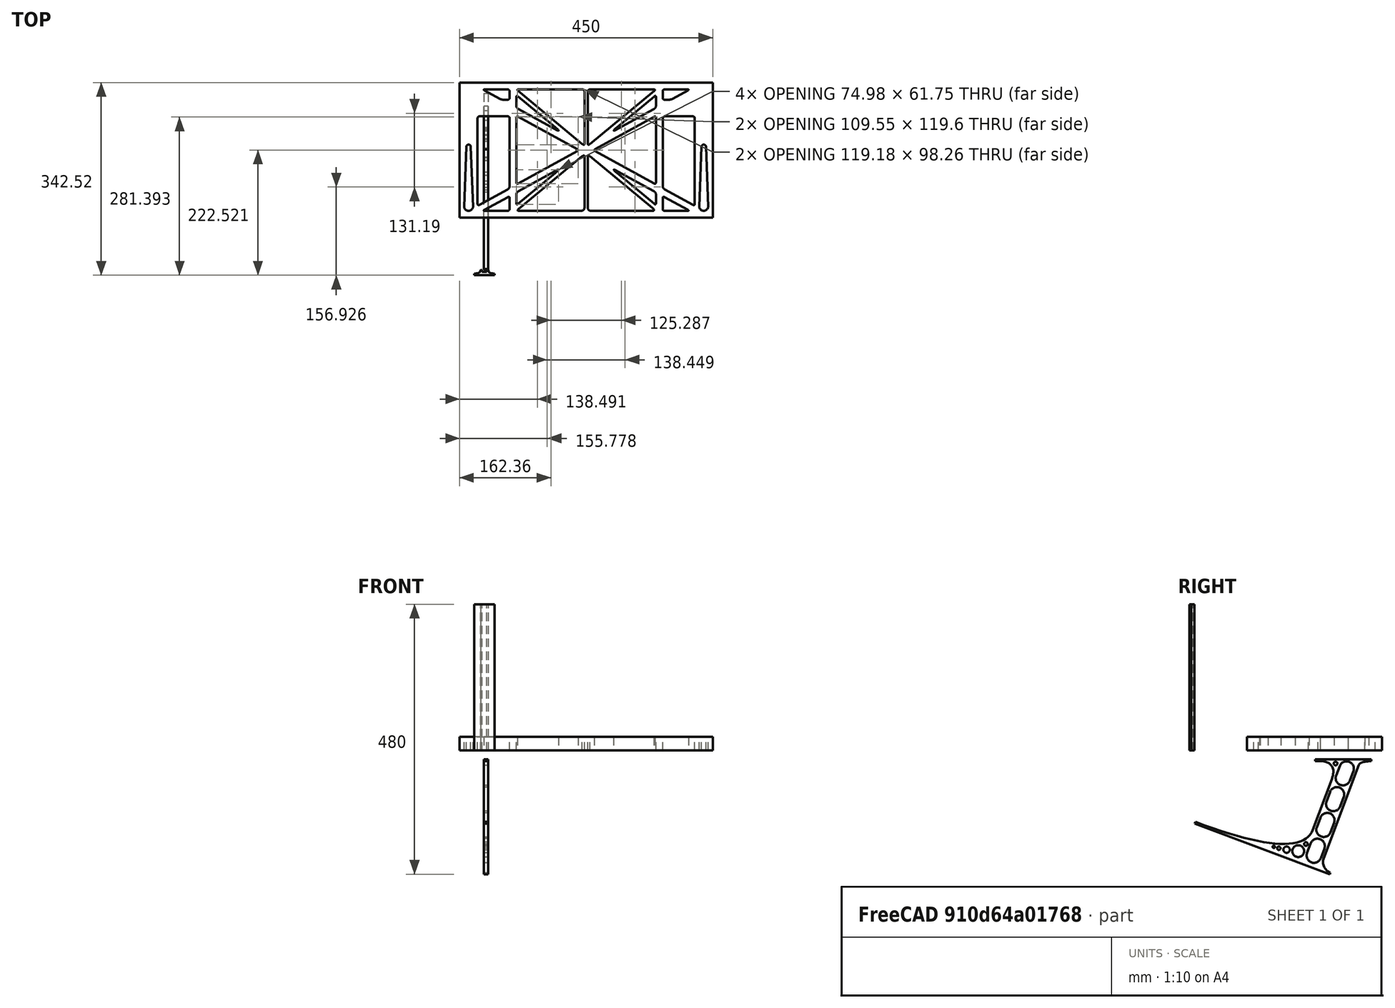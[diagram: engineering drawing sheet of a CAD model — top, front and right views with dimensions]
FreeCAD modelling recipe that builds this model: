
FCSTD DOCUMENT  (FreeCAD 0.19R0.19.2)
Label: laptopStand151FCStd
License: All rights reserved
LicenseURL: http://en.wikipedia.org/wiki/All_rights_reserved
objects: Sketcher::SketchObject×4, Part::Extrusion×3
note: 7 computed .brp shape members not serialized (recipe doc carries the construction recipe); baked Part::Feature solids carry a one-line shape summary decoded from their .brp

FEATURE [Sketcher::SketchObject] Sketch
  FullyConstrained = false
  sketch-geometry (349):
    g0: LineSegment StartX=-10.9272 StartY=-82.7794 StartZ=0 EndX=46.0728 EndY=-51.4823 EndZ=0
    g1: LineSegment StartX=-10.9272 StartY=76.4095 StartZ=0 EndX=-10.9272 EndY=-82.7794 EndZ=0
    g2: LineSegment StartX=46.0728 StartY=76.4095 StartZ=0 EndX=46.0728 EndY=-51.4823 EndZ=0
    g3: LineSegment StartX=-42.9272 StartY=136.221 StartZ=0 EndX=-42.9272 EndY=-103.779 EndZ=0
    g4: LineSegment StartX=407.073 StartY=136.221 StartZ=0 EndX=407.073 EndY=-103.779 EndZ=0
    g5: ArcOfCircle CenterX=-26.9272 CenterY=-83.7794 CenterZ=0 NormalX=0 NormalY=0 NormalZ=1 AngleXU=0 Radius=8 StartAngle=3.14159 EndAngle=6.28319
    g6: ArcOfCircle CenterX=391.073 CenterY=22.1087 CenterZ=0 NormalX=0 NormalY=0 NormalZ=1 AngleXU=0 Radius=8 StartAngle=-4.4e-15 EndAngle=3.14159
    g7: LineSegment StartX=399.073 StartY=22.1087 StartZ=0 EndX=399.073 EndY=-83.7794 EndZ=0
    g8: LineSegment StartX=383.073 StartY=22.1087 StartZ=0 EndX=383.073 EndY=-83.7794 EndZ=0
    g9: ArcOfCircle CenterX=391.073 CenterY=-83.7794 CenterZ=0 NormalX=0 NormalY=0 NormalZ=1 AngleXU=0 Radius=8 StartAngle=3.14159 EndAngle=6.28319
    g10: Circle CenterX=175.022 CenterY=27.0628 CenterZ=0 NormalX=0 NormalY=0 NormalZ=1 AngleXU=0 Radius=1
    g11: Circle CenterX=179.022 CenterY=24.8665 CenterZ=0 NormalX=0 NormalY=0 NormalZ=1 AngleXU=0 Radius=1
    g12: Circle CenterX=179.022 CenterY=27.0628 CenterZ=0 NormalX=0 NormalY=0 NormalZ=1 AngleXU=0 Radius=1
    g13: BSplineCurve PolesCount=3 KnotsCount=2 Degree=2 IsPeriodic=0
    g14: GeomPoint X=175.022 Y=27.0628 Z=0
    g15: GeomPoint X=179.022 Y=27.0628 Z=0
    g16: Circle CenterX=189.124 CenterY=27.0628 CenterZ=0 NormalX=0 NormalY=0 NormalZ=1 AngleXU=0 Radius=1
    g17: Circle CenterX=185.124 CenterY=24.8665 CenterZ=0 NormalX=0 NormalY=0 NormalZ=1 AngleXU=0 Radius=1
    g18: Circle CenterX=185.124 CenterY=27.0628 CenterZ=0 NormalX=0 NormalY=0 NormalZ=1 AngleXU=0 Radius=1
    g19: BSplineCurve PolesCount=3 KnotsCount=2 Degree=2 IsPeriodic=0
    g20: GeomPoint X=189.124 Y=27.0628 Z=0
    g21: GeomPoint X=185.124 Y=27.0628 Z=0
    g22: Circle CenterX=175.022 CenterY=5.37834 CenterZ=0 NormalX=0 NormalY=0 NormalZ=1 AngleXU=0 Radius=1
    g23: Circle CenterX=179.022 CenterY=7.57463 CenterZ=0 NormalX=0 NormalY=0 NormalZ=1 AngleXU=0 Radius=1
    g24: Circle CenterX=179.022 CenterY=5.34704 CenterZ=0 NormalX=0 NormalY=0 NormalZ=1 AngleXU=0 Radius=1
    g25: BSplineCurve PolesCount=3 KnotsCount=2 Degree=2 IsPeriodic=0
    g26: GeomPoint X=175.022 Y=5.37834 Z=0
    g27: GeomPoint X=179.022 Y=5.34704 Z=0
    g28: Circle CenterX=189.124 CenterY=5.37834 CenterZ=0 NormalX=0 NormalY=0 NormalZ=1 AngleXU=0 Radius=1
    g29: Circle CenterX=185.124 CenterY=7.57463 CenterZ=0 NormalX=0 NormalY=0 NormalZ=1 AngleXU=0 Radius=1
    g30: Circle CenterX=185.124 CenterY=5.34704 CenterZ=0 NormalX=0 NormalY=0 NormalZ=1 AngleXU=0 Radius=1
    g31: BSplineCurve PolesCount=3 KnotsCount=2 Degree=2 IsPeriodic=0
    g32: GeomPoint X=189.124 Y=5.37834 Z=0
    g33: GeomPoint X=185.124 Y=5.34704 Z=0
    g34: Circle CenterX=165.871 CenterY=18.1458 CenterZ=0 NormalX=0 NormalY=0 NormalZ=1 AngleXU=0 Radius=1
    g35: Circle CenterX=169.377 CenterY=16.2206 CenterZ=0 NormalX=0 NormalY=0 NormalZ=1 AngleXU=0 Radius=1
    g36: Circle CenterX=165.871 CenterY=14.2954 CenterZ=0 NormalX=0 NormalY=0 NormalZ=1 AngleXU=0 Radius=1
    g37: BSplineCurve PolesCount=3 KnotsCount=2 Degree=2 IsPeriodic=0
    g38: GeomPoint X=165.871 Y=18.1458 Z=0
    g39: GeomPoint X=165.871 Y=14.2954 Z=0
    g40: Circle CenterX=198.275 CenterY=18.1458 CenterZ=0 NormalX=0 NormalY=0 NormalZ=1 AngleXU=0 Radius=1
    g41: Circle CenterX=194.768 CenterY=16.2206 CenterZ=0 NormalX=0 NormalY=0 NormalZ=1 AngleXU=0 Radius=1
    g42: Circle CenterX=198.275 CenterY=14.2954 CenterZ=0 NormalX=0 NormalY=0 NormalZ=1 AngleXU=0 Radius=1
    g43: BSplineCurve PolesCount=3 KnotsCount=2 Degree=2 IsPeriodic=0
    g44: GeomPoint X=198.275 Y=18.1458 Z=0
    g45: GeomPoint X=198.275 Y=14.2954 Z=0
    g46: LineSegment StartX=407.073 StartY=-103.779 StartZ=0 EndX=-42.9272 EndY=-103.779 EndZ=0
    g47: LineSegment StartX=407.073 StartY=136.221 StartZ=0 EndX=-42.9272 EndY=136.221 EndZ=0
    g48: LineSegment StartX=46.0728 StartY=76.4095 StartZ=0 EndX=-10.9272 EndY=76.4095 EndZ=0
    g49: Circle CenterX=125.607 CenterY=54.1951 CenterZ=0 NormalX=0 NormalY=0 NormalZ=1 AngleXU=0 Radius=1
    g50: Circle CenterX=139.632 CenterY=46.4944 CenterZ=0 NormalX=0 NormalY=0 NormalZ=1 AngleXU=0 Radius=1
    g51: Circle CenterX=127.326 CenterY=56.7187 CenterZ=0 NormalX=0 NormalY=0 NormalZ=1 AngleXU=0 Radius=1
    g52: BSplineCurve PolesCount=3 KnotsCount=2 Degree=2 IsPeriodic=0
    g53: GeomPoint X=125.607 Y=54.1951 Z=0
    g54: GeomPoint X=127.326 Y=56.7187 Z=0
    g55: Circle CenterX=236.821 CenterY=56.7187 CenterZ=0 NormalX=0 NormalY=0 NormalZ=1 AngleXU=0 Radius=1
    g56: Circle CenterX=224.513 CenterY=46.4944 CenterZ=0 NormalX=0 NormalY=0 NormalZ=1 AngleXU=0 Radius=1
    g57: Circle CenterX=238.538 CenterY=54.1951 CenterZ=0 NormalX=0 NormalY=0 NormalZ=1 AngleXU=0 Radius=1
    g58: BSplineCurve PolesCount=3 KnotsCount=2 Degree=2 IsPeriodic=0
    g59: GeomPoint X=236.821 Y=56.7187 Z=0
    g60: GeomPoint X=238.538 Y=54.1951 Z=0
    g61: Circle CenterX=238.538 CenterY=-21.7539 CenterZ=0 NormalX=0 NormalY=0 NormalZ=1 AngleXU=0 Radius=1
    g62: Circle CenterX=224.513 CenterY=-14.0532 CenterZ=0 NormalX=0 NormalY=0 NormalZ=1 AngleXU=0 Radius=1
    g63: Circle CenterX=236.821 CenterY=-24.2775 CenterZ=0 NormalX=0 NormalY=0 NormalZ=1 AngleXU=0 Radius=1
    g64: BSplineCurve PolesCount=3 KnotsCount=2 Degree=2 IsPeriodic=0
    g65: GeomPoint X=238.538 Y=-21.7539 Z=0
    g66: GeomPoint X=236.821 Y=-24.2775 Z=0
    g67: Circle CenterX=125.607 CenterY=-21.7539 CenterZ=0 NormalX=0 NormalY=0 NormalZ=1 AngleXU=0 Radius=1
    g68: Circle CenterX=139.632 CenterY=-14.0532 CenterZ=0 NormalX=0 NormalY=0 NormalZ=1 AngleXU=0 Radius=1
    g69: Circle CenterX=127.325 CenterY=-24.2775 CenterZ=0 NormalX=0 NormalY=0 NormalZ=1 AngleXU=0 Radius=1
    g70: BSplineCurve PolesCount=3 KnotsCount=2 Degree=2 IsPeriodic=0
    g71: GeomPoint X=125.607 Y=-21.7539 Z=0
    g72: GeomPoint X=127.325 Y=-24.2775 Z=0
    g73: Circle CenterX=302.996 CenterY=111.695 CenterZ=0 NormalX=0 NormalY=0 NormalZ=1 AngleXU=0 Radius=1
    g74: Circle CenterX=306.073 CenterY=114.251 CenterZ=0 NormalX=0 NormalY=0 NormalZ=1 AngleXU=0 Radius=1
    g75: Circle CenterX=306.073 CenterY=110.251 CenterZ=0 NormalX=0 NormalY=0 NormalZ=1 AngleXU=0 Radius=1
    g76: BSplineCurve PolesCount=3 KnotsCount=2 Degree=2 IsPeriodic=0
    g77: GeomPoint X=302.996 Y=111.695 Z=0
    g78: GeomPoint X=306.073 Y=110.251 Z=0
    g79: Circle CenterX=306.073 CenterY=95.2763 CenterZ=0 NormalX=0 NormalY=0 NormalZ=1 AngleXU=0 Radius=1
    g80: Circle CenterX=306.073 CenterY=91.2763 CenterZ=0 NormalX=0 NormalY=0 NormalZ=1 AngleXU=0 Radius=1
    g81: Circle CenterX=302.567 CenterY=89.3511 CenterZ=0 NormalX=0 NormalY=0 NormalZ=1 AngleXU=0 Radius=1
    g82: BSplineCurve PolesCount=3 KnotsCount=2 Degree=2 IsPeriodic=0
    g83: GeomPoint X=306.073 Y=95.2763 Z=0
    g84: GeomPoint X=302.567 Y=89.3511 Z=0
    g85: LineSegment StartX=306.073 StartY=110.251 StartZ=0 EndX=306.073 EndY=95.2763 EndZ=0
    g86: LineSegment StartX=302.996 StartY=111.695 StartZ=0 EndX=236.821 EndY=56.7187 EndZ=0
    g87: LineSegment StartX=238.538 StartY=54.1951 StartZ=0 EndX=302.567 EndY=89.3511 EndZ=0
    g88: Circle CenterX=61.1496 CenterY=111.695 CenterZ=0 NormalX=0 NormalY=0 NormalZ=1 AngleXU=0 Radius=1
    g89: Circle CenterX=58.0728 CenterY=114.251 CenterZ=0 NormalX=0 NormalY=0 NormalZ=1 AngleXU=0 Radius=1
    g90: Circle CenterX=58.0728 CenterY=110.251 CenterZ=0 NormalX=0 NormalY=0 NormalZ=1 AngleXU=0 Radius=1
    g91: BSplineCurve PolesCount=3 KnotsCount=2 Degree=2 IsPeriodic=0
    g92: GeomPoint X=61.1496 Y=111.695 Z=0
    g93: GeomPoint X=58.0728 Y=110.251 Z=0
    g94: Circle CenterX=61.5791 CenterY=89.3511 CenterZ=0 NormalX=0 NormalY=0 NormalZ=1 AngleXU=0 Radius=1
    g95: Circle CenterX=58.0728 CenterY=91.2763 CenterZ=0 NormalX=0 NormalY=0 NormalZ=1 AngleXU=0 Radius=1
    g96: Circle CenterX=58.0728 CenterY=95.2763 CenterZ=0 NormalX=0 NormalY=0 NormalZ=1 AngleXU=0 Radius=1
    g97: BSplineCurve PolesCount=3 KnotsCount=2 Degree=2 IsPeriodic=0
    g98: GeomPoint X=61.5791 Y=89.3511 Z=0
    g99: GeomPoint X=58.0728 Y=95.2763 Z=0
    g100: LineSegment StartX=58.0728 StartY=110.251 StartZ=0 EndX=58.0728 EndY=95.2763 EndZ=0
    g101: LineSegment StartX=61.1496 StartY=111.695 StartZ=0 EndX=127.326 EndY=56.7187 EndZ=0
    g102: LineSegment StartX=125.607 StartY=54.1951 StartZ=0 EndX=61.5791 EndY=89.3511 EndZ=0
    g103: Circle CenterX=61.5791 CenterY=-56.9099 CenterZ=0 NormalX=0 NormalY=0 NormalZ=1 AngleXU=0 Radius=1
    g104: Circle CenterX=58.0728 CenterY=-58.8351 CenterZ=0 NormalX=0 NormalY=0 NormalZ=1 AngleXU=0 Radius=1
    g105: Circle CenterX=58.0728 CenterY=-62.8351 CenterZ=0 NormalX=0 NormalY=0 NormalZ=1 AngleXU=0 Radius=1
    g106: BSplineCurve PolesCount=3 KnotsCount=2 Degree=2 IsPeriodic=0
    g107: GeomPoint X=61.5791 Y=-56.9099 Z=0
    g108: GeomPoint X=58.0728 Y=-62.8351 Z=0
    g109: Circle CenterX=58.0728 CenterY=-77.8102 CenterZ=0 NormalX=0 NormalY=0 NormalZ=1 AngleXU=0 Radius=1
    g110: Circle CenterX=58.0728 CenterY=-81.8102 CenterZ=0 NormalX=0 NormalY=0 NormalZ=1 AngleXU=0 Radius=1
    g111: Circle CenterX=61.1496 CenterY=-79.2541 CenterZ=0 NormalX=0 NormalY=0 NormalZ=1 AngleXU=0 Radius=1
    g112: BSplineCurve PolesCount=3 KnotsCount=2 Degree=2 IsPeriodic=0
    g113: GeomPoint X=58.0728 Y=-77.8102 Z=0
    g114: GeomPoint X=61.1496 Y=-79.2541 Z=0
    g115: LineSegment StartX=58.0728 StartY=-62.8351 StartZ=0 EndX=58.0728 EndY=-77.8102 EndZ=0
    g116: LineSegment StartX=61.1496 StartY=-79.2541 StartZ=0 EndX=127.325 EndY=-24.2775 EndZ=0
    g117: LineSegment StartX=125.607 StartY=-21.7539 StartZ=0 EndX=61.5791 EndY=-56.9099 EndZ=0
    g118: Circle CenterX=302.567 CenterY=-56.9099 CenterZ=0 NormalX=0 NormalY=0 NormalZ=1 AngleXU=0 Radius=1
    g119: Circle CenterX=306.073 CenterY=-58.8351 CenterZ=0 NormalX=0 NormalY=0 NormalZ=1 AngleXU=0 Radius=1
    g120: Circle CenterX=306.073 CenterY=-62.8351 CenterZ=0 NormalX=0 NormalY=0 NormalZ=1 AngleXU=0 Radius=1
    g121: BSplineCurve PolesCount=3 KnotsCount=2 Degree=2 IsPeriodic=0
    g122: GeomPoint X=302.567 Y=-56.9099 Z=0
    g123: GeomPoint X=306.073 Y=-62.8351 Z=0
    g124: Circle CenterX=302.996 CenterY=-79.2541 CenterZ=0 NormalX=0 NormalY=0 NormalZ=1 AngleXU=0 Radius=1
    g125: Circle CenterX=306.073 CenterY=-81.8102 CenterZ=0 NormalX=0 NormalY=0 NormalZ=1 AngleXU=0 Radius=1
    g126: Circle CenterX=306.073 CenterY=-77.8102 CenterZ=0 NormalX=0 NormalY=0 NormalZ=1 AngleXU=0 Radius=1
    g127: BSplineCurve PolesCount=3 KnotsCount=2 Degree=2 IsPeriodic=0
    g128: GeomPoint X=302.996 Y=-79.2541 Z=0
    g129: GeomPoint X=306.073 Y=-77.8102 Z=0
    g130: LineSegment StartX=306.073 StartY=-62.8351 StartZ=0 EndX=306.073 EndY=-77.8102 EndZ=0
    g131: LineSegment StartX=302.996 StartY=-79.2541 StartZ=0 EndX=236.821 EndY=-24.2775 EndZ=0
    g132: LineSegment StartX=238.538 StartY=-21.7539 StartZ=0 EndX=302.567 EndY=-56.9099 EndZ=0
    g133: Circle CenterX=61.6457 CenterY=-88.8112 CenterZ=0 NormalX=0 NormalY=0 NormalZ=1 AngleXU=0 Radius=1
    g134: Circle CenterX=58.0728 CenterY=-91.7794 CenterZ=0 NormalX=0 NormalY=0 NormalZ=1 AngleXU=0 Radius=1
    g135: Circle CenterX=63.9135 CenterY=-91.7794 CenterZ=0 NormalX=0 NormalY=0 NormalZ=1 AngleXU=0 Radius=1
    g136: BSplineCurve PolesCount=3 KnotsCount=2 Degree=2 IsPeriodic=0
    g137: GeomPoint X=61.6457 Y=-88.8112 Z=0
    g138: GeomPoint X=63.9135 Y=-91.7794 Z=0
    g139: Circle CenterX=179.022 CenterY=-85.8163 CenterZ=0 NormalX=0 NormalY=0 NormalZ=1 AngleXU=0 Radius=1
    g140: Circle CenterX=179.022 CenterY=-91.7794 CenterZ=0 NormalX=0 NormalY=0 NormalZ=1 AngleXU=0 Radius=1
    g141: Circle CenterX=171.895 CenterY=-91.7794 CenterZ=0 NormalX=0 NormalY=0 NormalZ=1 AngleXU=0 Radius=1
    g142: BSplineCurve PolesCount=3 KnotsCount=2 Degree=2 IsPeriodic=0
    g143: GeomPoint X=179.022 Y=-85.8163 Z=0
    g144: GeomPoint X=171.895 Y=-91.7794 Z=0
    g145: Circle CenterX=185.124 CenterY=-86.2028 CenterZ=0 NormalX=0 NormalY=0 NormalZ=1 AngleXU=0 Radius=1
    g146: Circle CenterX=185.124 CenterY=-91.7794 CenterZ=0 NormalX=0 NormalY=0 NormalZ=1 AngleXU=0 Radius=1
    g147: Circle CenterX=191.747 CenterY=-91.7794 CenterZ=0 NormalX=0 NormalY=0 NormalZ=1 AngleXU=0 Radius=1
    g148: BSplineCurve PolesCount=3 KnotsCount=2 Degree=2 IsPeriodic=0
    g149: GeomPoint X=185.124 Y=-86.2028 Z=0
    g150: GeomPoint X=191.747 Y=-91.7794 Z=0
    g151: Circle CenterX=299.888 CenterY=-86.6413 CenterZ=0 NormalX=0 NormalY=0 NormalZ=1 AngleXU=0 Radius=1
    g152: Circle CenterX=306.073 CenterY=-91.7794 CenterZ=0 NormalX=0 NormalY=0 NormalZ=1 AngleXU=0 Radius=1
    g153: Circle CenterX=298.776 CenterY=-91.7794 CenterZ=0 NormalX=0 NormalY=0 NormalZ=1 AngleXU=0 Radius=1
    g154: BSplineCurve PolesCount=3 KnotsCount=2 Degree=2 IsPeriodic=0
    g155: GeomPoint X=299.888 Y=-86.6413 Z=0
    g156: GeomPoint X=298.776 Y=-91.7794 Z=0
    g157: LineSegment StartX=189.124 StartY=5.37834 StartZ=0 EndX=299.888 EndY=-86.6413 EndZ=0
    g158: LineSegment StartX=298.776 StartY=-91.7794 StartZ=0 EndX=191.747 EndY=-91.7794 EndZ=0
    g159: LineSegment StartX=185.124 StartY=-86.2028 StartZ=0 EndX=185.124 EndY=5.34704 EndZ=0
    g160: LineSegment StartX=179.022 StartY=5.34704 StartZ=0 EndX=179.022 EndY=-85.8163 EndZ=0
    g161: LineSegment StartX=171.895 StartY=-91.7794 StartZ=0 EndX=63.9135 EndY=-91.7794 EndZ=0
    g162: LineSegment StartX=61.6457 StartY=-88.8112 StartZ=0 EndX=175.022 EndY=5.37834 EndZ=0
    g163: Circle CenterX=302.073 CenterY=124.221 CenterZ=0 NormalX=0 NormalY=0 NormalZ=1 AngleXU=0 Radius=1
    g164: Circle CenterX=306.073 CenterY=124.221 CenterZ=0 NormalX=0 NormalY=0 NormalZ=1 AngleXU=0 Radius=1
    g165: Circle CenterX=302.996 CenterY=121.665 CenterZ=0 NormalX=0 NormalY=0 NormalZ=1 AngleXU=0 Radius=1
    g166: BSplineCurve PolesCount=3 KnotsCount=2 Degree=2 IsPeriodic=0
    g167: GeomPoint X=302.073 Y=124.221 Z=0
    g168: GeomPoint X=302.996 Y=121.665 Z=0
    g169: Circle CenterX=189.124 CenterY=124.221 CenterZ=0 NormalX=0 NormalY=0 NormalZ=1 AngleXU=0 Radius=1
    g170: Circle CenterX=185.124 CenterY=124.221 CenterZ=0 NormalX=0 NormalY=0 NormalZ=1 AngleXU=0 Radius=1
    g171: Circle CenterX=185.124 CenterY=120.221 CenterZ=0 NormalX=0 NormalY=0 NormalZ=1 AngleXU=0 Radius=1
    g172: BSplineCurve PolesCount=3 KnotsCount=2 Degree=2 IsPeriodic=0
    g173: GeomPoint X=189.124 Y=124.221 Z=0
    g174: GeomPoint X=185.124 Y=120.221 Z=0
    g175: Circle CenterX=175.022 CenterY=124.221 CenterZ=0 NormalX=0 NormalY=0 NormalZ=1 AngleXU=0 Radius=1
    g176: Circle CenterX=179.022 CenterY=124.221 CenterZ=0 NormalX=0 NormalY=0 NormalZ=1 AngleXU=0 Radius=1
    g177: Circle CenterX=179.022 CenterY=120.221 CenterZ=0 NormalX=0 NormalY=0 NormalZ=1 AngleXU=0 Radius=1
    g178: BSplineCurve PolesCount=3 KnotsCount=2 Degree=2 IsPeriodic=0
    g179: GeomPoint X=175.022 Y=124.221 Z=0
    g180: GeomPoint X=179.022 Y=120.221 Z=0
    g181: Circle CenterX=62.0728 CenterY=124.221 CenterZ=0 NormalX=0 NormalY=0 NormalZ=1 AngleXU=0 Radius=1
    g182: Circle CenterX=58.0728 CenterY=124.221 CenterZ=0 NormalX=0 NormalY=0 NormalZ=1 AngleXU=0 Radius=1
    g183: Circle CenterX=61.1496 CenterY=121.665 CenterZ=0 NormalX=0 NormalY=0 NormalZ=1 AngleXU=0 Radius=1
    g184: BSplineCurve PolesCount=3 KnotsCount=2 Degree=2 IsPeriodic=0
    g185: GeomPoint X=62.0728 Y=124.221 Z=0
    g186: GeomPoint X=61.1496 Y=121.665 Z=0
    g187: LineSegment StartX=62.0728 StartY=124.221 StartZ=0 EndX=175.022 EndY=124.221 EndZ=0
    g188: LineSegment StartX=179.022 StartY=120.221 StartZ=0 EndX=179.022 EndY=27.0628 EndZ=0
    g189: LineSegment StartX=185.124 StartY=27.0628 StartZ=0 EndX=185.124 EndY=120.221 EndZ=0
    g190: LineSegment StartX=189.124 StartY=124.221 StartZ=0 EndX=302.073 EndY=124.221 EndZ=0
    g191: LineSegment StartX=302.996 StartY=121.665 StartZ=0 EndX=189.124 EndY=27.0628 EndZ=0
    g192: LineSegment StartX=175.022 StartY=27.0628 StartZ=0 EndX=61.1496 EndY=121.665 EndZ=0
    g193: Circle CenterX=61.5791 CenterY=75.4095 CenterZ=0 NormalX=0 NormalY=0 NormalZ=1 AngleXU=0 Radius=1
    g194: Circle CenterX=58.0728 CenterY=77.3346 CenterZ=0 NormalX=0 NormalY=0 NormalZ=1 AngleXU=0 Radius=1
    g195: Circle CenterX=58.0728 CenterY=73.3346 CenterZ=0 NormalX=0 NormalY=0 NormalZ=1 AngleXU=0 Radius=1
    g196: BSplineCurve PolesCount=3 KnotsCount=2 Degree=2 IsPeriodic=0
    g197: GeomPoint X=61.5791 Y=75.4095 Z=0
    g198: GeomPoint X=58.0728 Y=73.3346 Z=0
    g199: Circle CenterX=58.0728 CenterY=-40.8935 CenterZ=0 NormalX=0 NormalY=0 NormalZ=1 AngleXU=0 Radius=1
    g200: Circle CenterX=58.0728 CenterY=-44.8935 CenterZ=0 NormalX=0 NormalY=0 NormalZ=1 AngleXU=0 Radius=1
    g201: Circle CenterX=61.5791 CenterY=-42.9683 CenterZ=0 NormalX=0 NormalY=0 NormalZ=1 AngleXU=0 Radius=1
    g202: BSplineCurve PolesCount=3 KnotsCount=2 Degree=2 IsPeriodic=0
    g203: GeomPoint X=58.0728 Y=-40.8935 Z=0
    g204: GeomPoint X=61.5791 Y=-42.9683 Z=0
    g205: LineSegment StartX=61.5791 StartY=-42.9683 StartZ=0 EndX=165.871 EndY=14.2954 EndZ=0
    g206: LineSegment StartX=165.871 StartY=18.1458 StartZ=0 EndX=61.5791 EndY=75.4095 EndZ=0
    g207: LineSegment StartX=58.0728 StartY=73.3346 StartZ=0 EndX=58.0728 EndY=-40.8935 EndZ=0
    g208: Circle CenterX=302.567 CenterY=-42.9683 CenterZ=0 NormalX=0 NormalY=0 NormalZ=1 AngleXU=0 Radius=1
    g209: Circle CenterX=306.073 CenterY=-44.8935 CenterZ=0 NormalX=0 NormalY=0 NormalZ=1 AngleXU=0 Radius=1
    g210: Circle CenterX=306.073 CenterY=-40.8935 CenterZ=0 NormalX=0 NormalY=0 NormalZ=1 AngleXU=0 Radius=1
    g211: BSplineCurve PolesCount=3 KnotsCount=2 Degree=2 IsPeriodic=0
    g212: GeomPoint X=302.567 Y=-42.9683 Z=0
    g213: GeomPoint X=306.073 Y=-40.8935 Z=0
    g214: Circle CenterX=306.073 CenterY=73.3346 CenterZ=0 NormalX=0 NormalY=0 NormalZ=1 AngleXU=0 Radius=1
    g215: Circle CenterX=306.073 CenterY=77.3346 CenterZ=0 NormalX=0 NormalY=0 NormalZ=1 AngleXU=0 Radius=1
    g216: Circle CenterX=302.567 CenterY=75.4095 CenterZ=0 NormalX=0 NormalY=0 NormalZ=1 AngleXU=0 Radius=1
    g217: BSplineCurve PolesCount=3 KnotsCount=2 Degree=2 IsPeriodic=0
    g218: GeomPoint X=306.073 Y=73.3346 Z=0
    g219: GeomPoint X=302.567 Y=75.4095 Z=0
    g220: LineSegment StartX=302.567 StartY=-42.9683 StartZ=0 EndX=198.275 EndY=14.2954 EndZ=0
    g221: LineSegment StartX=198.275 StartY=18.1458 StartZ=0 EndX=302.567 EndY=75.4095 EndZ=0
    g222: LineSegment StartX=306.073 StartY=73.3346 StartZ=0 EndX=306.073 EndY=-40.8935 EndZ=0
    g223: LineSegment StartX=322.073 StartY=105.865 StartZ=0 EndX=328.643 EndY=105.865 EndZ=0
    g224: LineSegment StartX=318.073 StartY=120.221 StartZ=0 EndX=318.073 EndY=109.865 EndZ=0
    g225: LineSegment StartX=336.157 StartY=107.779 StartZ=0 EndX=362.567 EndY=122.294 EndZ=0
    g226: Circle CenterX=362.073 CenterY=124.221 CenterZ=0 NormalX=0 NormalY=0 NormalZ=1 AngleXU=0 Radius=1
    g227: Circle CenterX=366.073 CenterY=124.221 CenterZ=0 NormalX=0 NormalY=0 NormalZ=1 AngleXU=0 Radius=1
    g228: Circle CenterX=362.567 CenterY=122.294 CenterZ=0 NormalX=0 NormalY=0 NormalZ=1 AngleXU=0 Radius=1
    g229: BSplineCurve PolesCount=3 KnotsCount=2 Degree=2 IsPeriodic=0
    g230: GeomPoint X=362.073 Y=124.221 Z=0
    g231: GeomPoint X=362.567 Y=122.294 Z=0
    g232: Circle CenterX=322.073 CenterY=124.221 CenterZ=0 NormalX=0 NormalY=0 NormalZ=1 AngleXU=0 Radius=1
    g233: Circle CenterX=318.073 CenterY=124.221 CenterZ=0 NormalX=0 NormalY=0 NormalZ=1 AngleXU=0 Radius=1
    g234: Circle CenterX=318.073 CenterY=120.221 CenterZ=0 NormalX=0 NormalY=0 NormalZ=1 AngleXU=0 Radius=1
    g235: BSplineCurve PolesCount=3 KnotsCount=2 Degree=2 IsPeriodic=0
    g236: GeomPoint X=322.073 Y=124.221 Z=0
    g237: GeomPoint X=318.073 Y=120.221 Z=0
    g238: Circle CenterX=322.073 CenterY=105.865 CenterZ=0 NormalX=0 NormalY=0 NormalZ=1 AngleXU=0 Radius=1
    g239: Circle CenterX=318.073 CenterY=105.865 CenterZ=0 NormalX=0 NormalY=0 NormalZ=1 AngleXU=0 Radius=1
    g240: Circle CenterX=318.073 CenterY=109.865 CenterZ=0 NormalX=0 NormalY=0 NormalZ=1 AngleXU=0 Radius=1
    g241: BSplineCurve PolesCount=3 KnotsCount=2 Degree=2 IsPeriodic=0
    g242: GeomPoint X=322.073 Y=105.865 Z=0
    g243: GeomPoint X=318.073 Y=109.865 Z=0
    g244: Circle CenterX=336.157 CenterY=107.779 CenterZ=0 NormalX=0 NormalY=0 NormalZ=1 AngleXU=0 Radius=1
    g245: Circle CenterX=332.651 CenterY=105.853 CenterZ=0 NormalX=0 NormalY=0 NormalZ=1 AngleXU=0 Radius=1
    g246: Circle CenterX=328.643 CenterY=105.865 CenterZ=0 NormalX=0 NormalY=0 NormalZ=1 AngleXU=0 Radius=1
    g247: BSplineCurve PolesCount=3 KnotsCount=2 Degree=2 IsPeriodic=0
    g248: GeomPoint X=336.157 Y=107.779 Z=0
    g249: GeomPoint X=328.643 Y=105.865 Z=0
    g250: LineSegment StartX=322.073 StartY=124.221 StartZ=0 EndX=362.073 EndY=124.221 EndZ=0
    g251: Circle CenterX=371.567 CenterY=-80.8644 CenterZ=0 NormalX=0 NormalY=0 NormalZ=1 AngleXU=0 Radius=1
    g252: Circle CenterX=375.073 CenterY=-82.7896 CenterZ=0 NormalX=0 NormalY=0 NormalZ=1 AngleXU=0 Radius=1
    g253: Circle CenterX=375.073 CenterY=-78.7896 CenterZ=0 NormalX=0 NormalY=0 NormalZ=1 AngleXU=0 Radius=1
    g254: BSplineCurve PolesCount=3 KnotsCount=2 Degree=2 IsPeriodic=0
    g255: GeomPoint X=371.567 Y=-80.8644 Z=0
    g256: GeomPoint X=375.073 Y=-78.7896 Z=0
    g257: Circle CenterX=321.579 CenterY=-53.4075 CenterZ=0 NormalX=0 NormalY=0 NormalZ=1 AngleXU=0 Radius=1
    g258: Circle CenterX=318.073 CenterY=-51.4823 CenterZ=0 NormalX=0 NormalY=0 NormalZ=1 AngleXU=0 Radius=1
    g259: Circle CenterX=318.073 CenterY=-47.4805 CenterZ=0 NormalX=0 NormalY=0 NormalZ=1 AngleXU=0 Radius=1
    g260: BSplineCurve PolesCount=3 KnotsCount=2 Degree=2 IsPeriodic=0
    g261: GeomPoint X=321.579 Y=-53.4075 Z=0
    g262: GeomPoint X=318.073 Y=-47.4805 Z=0
    g263: LineSegment StartX=371.567 StartY=-80.8644 StartZ=0 EndX=321.579 EndY=-53.4075 EndZ=0
    g264: Circle CenterX=321.579 CenterY=-67.3492 CenterZ=0 NormalX=0 NormalY=0 NormalZ=1 AngleXU=0 Radius=1
    g265: Circle CenterX=318.073 CenterY=-65.424 CenterZ=0 NormalX=0 NormalY=0 NormalZ=1 AngleXU=0 Radius=1
    g266: Circle CenterX=318.073 CenterY=-69.424 CenterZ=0 NormalX=0 NormalY=0 NormalZ=1 AngleXU=0 Radius=1
    g267: BSplineCurve PolesCount=3 KnotsCount=2 Degree=2 IsPeriodic=0
    g268: GeomPoint X=321.579 Y=-67.3492 Z=0
    g269: GeomPoint X=318.073 Y=-69.424 Z=0
    g270: Circle CenterX=362.567 CenterY=-89.8542 CenterZ=0 NormalX=0 NormalY=0 NormalZ=1 AngleXU=0 Radius=1
    g271: Circle CenterX=366.073 CenterY=-91.7794 CenterZ=0 NormalX=0 NormalY=0 NormalZ=1 AngleXU=0 Radius=1
    g272: Circle CenterX=362.073 CenterY=-91.7794 CenterZ=0 NormalX=0 NormalY=0 NormalZ=1 AngleXU=0 Radius=1
    g273: BSplineCurve PolesCount=3 KnotsCount=2 Degree=2 IsPeriodic=0
    g274: GeomPoint X=362.567 Y=-89.8542 Z=0
    g275: GeomPoint X=362.073 Y=-91.7794 Z=0
    g276: Circle CenterX=322.073 CenterY=-91.7794 CenterZ=0 NormalX=0 NormalY=0 NormalZ=1 AngleXU=0 Radius=1
    g277: Circle CenterX=318.073 CenterY=-91.7794 CenterZ=0 NormalX=0 NormalY=0 NormalZ=1 AngleXU=0 Radius=1
    g278: Circle CenterX=318.073 CenterY=-87.7794 CenterZ=0 NormalX=0 NormalY=0 NormalZ=1 AngleXU=0 Radius=1
    g279: BSplineCurve PolesCount=3 KnotsCount=2 Degree=2 IsPeriodic=0
    g280: GeomPoint X=322.073 Y=-91.7794 Z=0
    g281: GeomPoint X=318.073 Y=-87.7794 Z=0
    g282: LineSegment StartX=362.567 StartY=-89.8542 StartZ=0 EndX=321.579 EndY=-67.3492 EndZ=0
    g283: LineSegment StartX=318.073 StartY=-69.424 StartZ=0 EndX=318.073 EndY=-87.7794 EndZ=0
    g284: LineSegment StartX=322.073 StartY=-91.7794 StartZ=0 EndX=362.073 EndY=-91.7794 EndZ=0
    g285: Circle CenterX=2.07281 CenterY=124.221 CenterZ=0 NormalX=0 NormalY=0 NormalZ=1 AngleXU=0 Radius=1
    g286: Circle CenterX=1.57905 CenterY=122.295 CenterZ=0 NormalX=0 NormalY=0 NormalZ=1 AngleXU=0 Radius=1
    g287: BSplineCurve PolesCount=3 KnotsCount=2 Degree=2 IsPeriodic=0
    g288: GeomPoint X=2.07281 Y=124.221 Z=0
    g289: GeomPoint X=1.57905 Y=122.295 Z=0
    g290: Circle CenterX=42.0728 CenterY=124.221 CenterZ=0 NormalX=0 NormalY=0 NormalZ=1 AngleXU=0 Radius=1
    g291: Circle CenterX=46.0728 CenterY=124.221 CenterZ=0 NormalX=0 NormalY=0 NormalZ=1 AngleXU=0 Radius=1
    g292: Circle CenterX=46.0728 CenterY=120.221 CenterZ=0 NormalX=0 NormalY=0 NormalZ=1 AngleXU=0 Radius=1
    g293: BSplineCurve PolesCount=3 KnotsCount=2 Degree=2 IsPeriodic=0
    g294: GeomPoint X=42.0728 Y=124.221 Z=0
    g295: GeomPoint X=46.0728 Y=120.221 Z=0
    g296: Circle CenterX=46.0728 CenterY=109.865 CenterZ=0 NormalX=0 NormalY=0 NormalZ=1 AngleXU=0 Radius=1
    g297: Circle CenterX=46.0728 CenterY=105.865 CenterZ=0 NormalX=0 NormalY=0 NormalZ=1 AngleXU=0 Radius=1
    g298: Circle CenterX=42.0728 CenterY=105.865 CenterZ=0 NormalX=0 NormalY=0 NormalZ=1 AngleXU=0 Radius=1
    g299: BSplineCurve PolesCount=3 KnotsCount=2 Degree=2 IsPeriodic=0
    g300: GeomPoint X=46.0728 Y=109.865 Z=0
    g301: GeomPoint X=42.0728 Y=105.865 Z=0
    g302: Circle CenterX=35.5028 CenterY=105.865 CenterZ=0 NormalX=0 NormalY=0 NormalZ=1 AngleXU=0 Radius=1
    g303: Circle CenterX=31.5028 CenterY=105.865 CenterZ=0 NormalX=0 NormalY=0 NormalZ=1 AngleXU=0 Radius=1
    g304: Circle CenterX=27.9965 CenterY=107.79 CenterZ=0 NormalX=0 NormalY=0 NormalZ=1 AngleXU=0 Radius=1
    g305: BSplineCurve PolesCount=3 KnotsCount=2 Degree=2 IsPeriodic=0
    g306: GeomPoint X=35.5028 Y=105.865 Z=0
    g307: GeomPoint X=27.9965 Y=107.79 Z=0
    g308: LineSegment StartX=2.07281 StartY=124.221 StartZ=0 EndX=42.0728 EndY=124.221 EndZ=0
    g309: LineSegment StartX=46.0728 StartY=120.221 StartZ=0 EndX=46.0728 EndY=109.865 EndZ=0
    g310: LineSegment StartX=42.0728 StartY=105.865 StartZ=0 EndX=35.5028 EndY=105.865 EndZ=0
    g311: LineSegment StartX=27.9965 StartY=107.79 StartZ=0 EndX=1.57905 EndY=122.295 EndZ=0
    g312: Circle CenterX=42.5666 CenterY=-67.3492 CenterZ=0 NormalX=0 NormalY=0 NormalZ=1 AngleXU=0 Radius=1
    g313: Circle CenterX=46.0728 CenterY=-65.424 CenterZ=0 NormalX=0 NormalY=0 NormalZ=1 AngleXU=0 Radius=1
    g314: Circle CenterX=46.0728 CenterY=-69.424 CenterZ=0 NormalX=0 NormalY=0 NormalZ=1 AngleXU=0 Radius=1
    g315: BSplineCurve PolesCount=3 KnotsCount=2 Degree=2 IsPeriodic=0
    g316: GeomPoint X=42.5666 Y=-67.3492 Z=0
    g317: GeomPoint X=46.0728 Y=-69.424 Z=0
    g318: Circle CenterX=46.0728 CenterY=-87.7794 CenterZ=0 NormalX=0 NormalY=0 NormalZ=1 AngleXU=0 Radius=1
    g319: Circle CenterX=46.0728 CenterY=-91.7794 CenterZ=0 NormalX=0 NormalY=0 NormalZ=1 AngleXU=0 Radius=1
    g320: Circle CenterX=42.0728 CenterY=-91.7794 CenterZ=0 NormalX=0 NormalY=0 NormalZ=1 AngleXU=0 Radius=1
    g321: BSplineCurve PolesCount=3 KnotsCount=2 Degree=2 IsPeriodic=0
    g322: GeomPoint X=46.0728 Y=-87.7794 Z=0
    g323: GeomPoint X=42.0728 Y=-91.7794 Z=0
    g324: Circle CenterX=2.07281 CenterY=-91.7794 CenterZ=0 NormalX=0 NormalY=0 NormalZ=1 AngleXU=0 Radius=1
    g325: Circle CenterX=-1.92719 CenterY=-91.7794 CenterZ=0 NormalX=0 NormalY=0 NormalZ=1 AngleXU=0 Radius=1
    g326: Circle CenterX=1.57905 CenterY=-89.8542 CenterZ=0 NormalX=0 NormalY=0 NormalZ=1 AngleXU=0 Radius=1
    g327: BSplineCurve PolesCount=3 KnotsCount=2 Degree=2 IsPeriodic=0
    g328: GeomPoint X=2.07281 Y=-91.7794 Z=0
    g329: GeomPoint X=1.57905 Y=-89.8542 Z=0
    g330: LineSegment StartX=2.07281 StartY=-91.7794 StartZ=0 EndX=42.0728 EndY=-91.7794 EndZ=0
    g331: LineSegment StartX=46.0728 StartY=-87.7794 StartZ=0 EndX=46.0728 EndY=-69.424 EndZ=0
    g332: LineSegment StartX=42.5666 StartY=-67.3492 StartZ=0 EndX=1.57905 EndY=-89.8542 EndZ=0
    g333: Circle CenterX=322.073 CenterY=76.4095 CenterZ=0 NormalX=0 NormalY=0 NormalZ=1 AngleXU=0 Radius=4
    g334: BSplineCurve PolesCount=3 KnotsCount=2 Degree=2 IsPeriodic=0
    g335: GeomPoint X=318.073 Y=72.4095 Z=0
    g336: GeomPoint X=322.073 Y=76.4095 Z=0
    g337: Circle CenterX=375.073 CenterY=72.4095 CenterZ=0 NormalX=0 NormalY=0 NormalZ=1 AngleXU=0 Radius=1
    g338: Circle CenterX=375.073 CenterY=76.4095 CenterZ=0 NormalX=0 NormalY=0 NormalZ=1 AngleXU=0 Radius=1
    g339: Circle CenterX=371.073 CenterY=76.4095 CenterZ=0 NormalX=0 NormalY=0 NormalZ=1 AngleXU=0 Radius=1
    g340: BSplineCurve PolesCount=3 KnotsCount=2 Degree=2 IsPeriodic=0
    g341: GeomPoint X=375.073 Y=72.4095 Z=0
    g342: GeomPoint X=371.073 Y=76.4095 Z=0
    g343: LineSegment StartX=322.073 StartY=76.4095 StartZ=0 EndX=371.073 EndY=76.4095 EndZ=0
    g344: LineSegment StartX=318.073 StartY=72.4095 StartZ=0 EndX=318.073 EndY=-47.4805 EndZ=0
    g345: LineSegment StartX=375.073 StartY=72.4095 StartZ=0 EndX=375.073 EndY=-78.7896 EndZ=0
    g346: ArcOfCircle CenterX=-26.9272 CenterY=22.1087 CenterZ=0 NormalX=0 NormalY=0 NormalZ=1 AngleXU=0 Radius=4 StartAngle=5e-16 EndAngle=3.14159
    g347: LineSegment StartX=-30.9272 StartY=22.1087 StartZ=0 EndX=-34.9272 EndY=-83.7794 EndZ=0
    g348: LineSegment StartX=-18.9272 StartY=-83.7794 StartZ=0 EndX=-22.9272 EndY=22.1087 EndZ=0
  constraints (572):
    c: Coincident(g0,g2)
    c: Block(g0)
    c: Block(g1)
    c: Vertical(g3)
    c: Vertical(g4)
    c: Block(g4)
    c: Block(g3)
    c: Tangent(g6,g7) = 1.5708
    c: Tangent(g7,g9) = 1.5708
    c: Equal(g6,g9)
    c: Coincident(g8,g6)
    c: Coincident(g8,g9)
    c: Block(g7)
    c: Block(g8)
    c: Weight(g10) = 1
    c: Equal(g10,g11)
    c: Equal(g10,g12)
    c: InternalAlignment(g10,g13)
    c: InternalAlignment(g11,g13)
    c: InternalAlignment(g12,g13)
    c: InternalAlignment(g14,g13)
    c: InternalAlignment(g15,g13)
    c: Weight(g16) = 1
    c: Equal(g16,g17)
    c: Equal(g16,g18)
    c: InternalAlignment(g16,g19)
    c: InternalAlignment(g17,g19)
    c: InternalAlignment(g18,g19)
    c: InternalAlignment(g20,g19)
    c: InternalAlignment(g21,g19)
    c: Block(g19)
    c: Block(g13)
    c: Weight(g22) = 1
    c: Equal(g22,g23)
    c: Equal(g22,g24)
    c: InternalAlignment(g22,g25)
    c: InternalAlignment(g23,g25)
    c: InternalAlignment(g24,g25)
    c: InternalAlignment(g26,g25)
    c: InternalAlignment(g27,g25)
    c: Weight(g28) = 1
    c: Equal(g28,g29)
    c: Equal(g28,g30)
    c: InternalAlignment(g28,g31)
    c: InternalAlignment(g29,g31)
    c: InternalAlignment(g30,g31)
    c: InternalAlignment(g32,g31)
    c: InternalAlignment(g33,g31)
    c: Block(g31)
    c: Block(g25)
    c: Weight(g34) = 1
    c: Equal(g34,g35)
    c: Equal(g34,g36)
    c: InternalAlignment(g34,g37)
    c: InternalAlignment(g35,g37)
    c: InternalAlignment(g36,g37)
    c: InternalAlignment(g38,g37)
    c: InternalAlignment(g39,g37)
    c: Weight(g40) = 1
    c: Equal(g40,g41)
    c: Equal(g40,g42)
    c: InternalAlignment(g40,g43)
    c: InternalAlignment(g41,g43)
    c: InternalAlignment(g42,g43)
    c: InternalAlignment(g44,g43)
    c: InternalAlignment(g45,g43)
    c: Block(g37)
    c: Block(g43)
    c: Coincident(g46,g4)
    c: Coincident(g46,g3)
    c: Horizontal(g46)
    c: Distance(g46) = 450
    c: Coincident(g47,g4)
    c: Coincident(g47,g3)
    c: Horizontal(g47)
    c: Horizontal(g48)
    c: Coincident(g2,g48)
    c: Block(g48)
    c: Coincident(g1,g48)
    c: Weight(g49) = 1
    c: Equal(g49,g50)
    c: Equal(g49,g51)
    c: InternalAlignment(g49,g52)
    c: InternalAlignment(g50,g52)
    c: InternalAlignment(g51,g52)
    c: InternalAlignment(g53,g52)
    c: InternalAlignment(g54,g52)
    c: Block(g52)
    c: Weight(g55) = 1
    c: Equal(g55,g56)
    c: Equal(g55,g57)
    c: InternalAlignment(g55,g58)
    c: InternalAlignment(g56,g58)
    c: InternalAlignment(g57,g58)
    c: InternalAlignment(g59,g58)
    c: InternalAlignment(g60,g58)
    c: Block(g58)
    c: Weight(g61) = 1
    c: Equal(g61,g62)
    c: Equal(g61,g63)
    c: InternalAlignment(g61,g64)
    c: InternalAlignment(g62,g64)
    c: InternalAlignment(g63,g64)
    c: InternalAlignment(g65,g64)
    c: InternalAlignment(g66,g64)
    c: Block(g64)
    c: Weight(g67) = 1
    c: Equal(g67,g68)
    c: Equal(g67,g69)
    c: InternalAlignment(g67,g70)
    c: InternalAlignment(g68,g70)
    c: InternalAlignment(g69,g70)
    c: InternalAlignment(g71,g70)
    c: InternalAlignment(g72,g70)
    c: Block(g70)
    c: Weight(g73) = 1
    c: Equal(g73,g74)
    c: Equal(g73,g75)
    c: InternalAlignment(g73,g76)
    c: InternalAlignment(g74,g76)
    c: InternalAlignment(g75,g76)
    c: InternalAlignment(g77,g76)
    c: InternalAlignment(g78,g76)
    c: Weight(g79) = 1
    c: Equal(g79,g80)
    c: Equal(g79,g81)
    c: InternalAlignment(g79,g82)
    c: InternalAlignment(g80,g82)
    c: InternalAlignment(g81,g82)
    c: InternalAlignment(g83,g82)
    c: InternalAlignment(g84,g82)
    c: Block(g76)
    c: Block(g82)
    c: Coincident(g85,g76)
    c: Coincident(g85,g82)
    c: Vertical(g85)
    c: Coincident(g86,g76)
    c: Coincident(g86,g58)
    c: Coincident(g87,g58)
    c: Coincident(g87,g82)
    c: Weight(g88) = 1
    c: Equal(g88,g89)
    c: Equal(g88,g90)
    c: InternalAlignment(g88,g91)
    c: InternalAlignment(g89,g91)
    c: InternalAlignment(g90,g91)
    c: InternalAlignment(g92,g91)
    c: InternalAlignment(g93,g91)
    c: Weight(g94) = 1
    c: Equal(g94,g95)
    c: Equal(g94,g96)
    c: InternalAlignment(g94,g97)
    c: InternalAlignment(g95,g97)
    c: InternalAlignment(g96,g97)
    c: InternalAlignment(g98,g97)
    c: InternalAlignment(g99,g97)
    c: Block(g91)
    c: Block(g97)
    c: Coincident(g100,g91)
    c: Coincident(g100,g97)
    c: Vertical(g100)
    c: Coincident(g101,g91)
    c: Coincident(g101,g52)
    c: Coincident(g102,g52)
    c: Coincident(g102,g97)
    c: Weight(g103) = 1
    c: Equal(g103,g104)
    c: Equal(g103,g105)
    c: InternalAlignment(g103,g106)
    c: InternalAlignment(g104,g106)
    c: InternalAlignment(g105,g106)
    c: InternalAlignment(g107,g106)
    c: InternalAlignment(g108,g106)
    c: Weight(g109) = 1
    c: Equal(g109,g110)
    c: Equal(g109,g111)
    c: InternalAlignment(g109,g112)
    c: InternalAlignment(g110,g112)
    c: InternalAlignment(g111,g112)
    c: InternalAlignment(g113,g112)
    c: InternalAlignment(g114,g112)
    c: Block(g106)
    c: Block(g112)
    c: Coincident(g115,g106)
    c: Coincident(g115,g112)
    c: Vertical(g115)
    c: Coincident(g116,g112)
    c: Coincident(g116,g70)
    c: Coincident(g117,g70)
    c: Coincident(g117,g106)
    c: Weight(g118) = 1
    c: Equal(g118,g119)
    c: Equal(g118,g120)
    c: InternalAlignment(g118,g121)
    c: InternalAlignment(g119,g121)
    c: InternalAlignment(g120,g121)
    c: InternalAlignment(g122,g121)
    c: InternalAlignment(g123,g121)
    c: Weight(g124) = 1
    c: Equal(g124,g125)
    c: Equal(g124,g126)
    c: InternalAlignment(g124,g127)
    c: InternalAlignment(g125,g127)
    c: InternalAlignment(g126,g127)
    c: InternalAlignment(g128,g127)
    c: InternalAlignment(g129,g127)
    c: Block(g121)
    c: Block(g127)
    c: Coincident(g130,g121)
    c: Coincident(g130,g127)
    c: Vertical(g130)
    c: Coincident(g131,g127)
    c: Coincident(g131,g64)
    c: Coincident(g132,g64)
    c: Coincident(g132,g121)
    c: Weight(g133) = 1
    c: Equal(g133,g134)
    c: Equal(g133,g135)
    c: InternalAlignment(g133,g136)
    c: InternalAlignment(g134,g136)
    c: InternalAlignment(g135,g136)
    c: InternalAlignment(g137,g136)
    c: InternalAlignment(g138,g136)
    c: Weight(g139) = 1
    c: Equal(g139,g140)
    c: Equal(g139,g141)
    c: InternalAlignment(g139,g142)
    c: InternalAlignment(g140,g142)
    c: InternalAlignment(g141,g142)
    c: InternalAlignment(g143,g142)
    c: InternalAlignment(g144,g142)
    c: Weight(g145) = 1
    c: Equal(g145,g146)
    c: Equal(g145,g147)
    c: InternalAlignment(g145,g148)
    c: InternalAlignment(g146,g148)
    c: InternalAlignment(g147,g148)
    c: InternalAlignment(g149,g148)
    c: InternalAlignment(g150,g148)
    c: Weight(g151) = 1
    c: Equal(g151,g152)
    c: Equal(g151,g153)
    c: InternalAlignment(g151,g154)
    c: InternalAlignment(g152,g154)
    c: InternalAlignment(g153,g154)
    c: InternalAlignment(g155,g154)
    c: InternalAlignment(g156,g154)
    c: Block(g154)
    c: Block(g148)
    c: Block(g142)
    c: Block(g136)
    c: Coincident(g157,g31)
    c: Coincident(g157,g154)
    c: Coincident(g158,g154)
    c: Coincident(g158,g148)
    c: Horizontal(g158)
    c: Coincident(g159,g148)
    c: Coincident(g159,g31)
    c: Vertical(g159)
    c: Coincident(g160,g25)
    c: Coincident(g160,g142)
    c: Vertical(g160)
    c: Coincident(g161,g142)
    c: Coincident(g161,g136)
    c: Horizontal(g161)
    c: Coincident(g162,g136)
    c: Coincident(g162,g25)
    c: Weight(g163) = 1
    c: Equal(g163,g164)
    c: Equal(g163,g165)
    c: InternalAlignment(g163,g166)
    c: InternalAlignment(g164,g166)
    c: InternalAlignment(g165,g166)
    c: InternalAlignment(g167,g166)
    c: InternalAlignment(g168,g166)
    c: Weight(g169) = 1
    c: Equal(g169,g170)
    c: Equal(g169,g171)
    c: InternalAlignment(g169,g172)
    c: InternalAlignment(g170,g172)
    c: InternalAlignment(g171,g172)
    c: InternalAlignment(g173,g172)
    c: InternalAlignment(g174,g172)
    c: Weight(g175) = 1
    c: Equal(g175,g176)
    c: Equal(g175,g177)
    c: InternalAlignment(g175,g178)
    c: InternalAlignment(g176,g178)
    c: InternalAlignment(g177,g178)
    c: InternalAlignment(g179,g178)
    c: InternalAlignment(g180,g178)
    c: Weight(g181) = 1
    c: Equal(g181,g182)
    c: Equal(g181,g183)
    c: InternalAlignment(g181,g184)
    c: InternalAlignment(g182,g184)
    c: InternalAlignment(g183,g184)
    c: InternalAlignment(g185,g184)
    c: InternalAlignment(g186,g184)
    c: Block(g184)
    c: Block(g178)
    c: Block(g172)
    c: Block(g166)
    c: Coincident(g187,g184)
    c: Coincident(g187,g178)
    c: Horizontal(g187)
    c: Coincident(g188,g178)
    c: Coincident(g188,g13)
    c: Vertical(g188)
    c: Coincident(g189,g19)
    c: Coincident(g189,g172)
    c: Vertical(g189)
    c: Coincident(g190,g172)
    c: Coincident(g190,g166)
    c: Horizontal(g190)
    c: Coincident(g191,g166)
    c: Coincident(g191,g19)
    c: Coincident(g192,g13)
    c: Weight(g193) = 1
    c: Equal(g193,g194)
    c: Equal(g193,g195)
    c: InternalAlignment(g193,g196)
    c: InternalAlignment(g194,g196)
    c: InternalAlignment(g195,g196)
    c: InternalAlignment(g197,g196)
    c: InternalAlignment(g198,g196)
    c: Weight(g199) = 1
    c: Equal(g199,g200)
    c: Equal(g199,g201)
    c: InternalAlignment(g199,g202)
    c: InternalAlignment(g200,g202)
    c: InternalAlignment(g201,g202)
    c: InternalAlignment(g203,g202)
    c: InternalAlignment(g204,g202)
    c: Block(g202)
    c: Block(g196)
    c: Coincident(g205,g202)
    c: Coincident(g205,g37)
    c: Coincident(g206,g37)
    c: Coincident(g206,g196)
    c: Coincident(g207,g196)
    c: Coincident(g207,g202)
    c: Vertical(g207)
    c: Weight(g208) = 1
    c: Equal(g208,g209)
    c: Equal(g208,g210)
    c: InternalAlignment(g208,g211)
    c: InternalAlignment(g209,g211)
    c: InternalAlignment(g210,g211)
    c: InternalAlignment(g212,g211)
    c: InternalAlignment(g213,g211)
    c: Weight(g214) = 1
    c: Equal(g214,g215)
    c: Equal(g214,g216)
    c: InternalAlignment(g214,g217)
    c: InternalAlignment(g215,g217)
    c: InternalAlignment(g216,g217)
    c: InternalAlignment(g218,g217)
    c: InternalAlignment(g219,g217)
    c: Block(g217)
    c: Block(g211)
    c: Coincident(g220,g211)
    c: Coincident(g220,g43)
    c: Coincident(g221,g43)
    c: Coincident(g221,g217)
    c: Coincident(g222,g217)
    c: Coincident(g222,g211)
    c: Vertical(g222)
    c: Horizontal(g223)
    c: Block(g223)
    c: Vertical(g224)
    c: Block(g224)
    c: Block(g225)
    c: Weight(g226) = 1
    c: Equal(g226,g227)
    c: Equal(g226,g228)
    c: InternalAlignment(g226,g229)
    c: InternalAlignment(g227,g229)
    c: InternalAlignment(g228,g229)
    c: InternalAlignment(g230,g229)
    c: InternalAlignment(g231,g229)
    c: Weight(g232) = 1
    c: Equal(g232,g233)
    c: Equal(g232,g234)
    c: InternalAlignment(g232,g235)
    c: InternalAlignment(g233,g235)
    c: InternalAlignment(g234,g235)
    c: InternalAlignment(g236,g235)
    c: InternalAlignment(g237,g235)
    c: Weight(g238) = 1
    c: Equal(g238,g239)
    c: Equal(g238,g240)
    c: InternalAlignment(g238,g241)
    c: InternalAlignment(g239,g241)
    c: InternalAlignment(g240,g241)
    c: InternalAlignment(g242,g241)
    c: InternalAlignment(g243,g241)
    c: Weight(g244) = 1
    c: Equal(g244,g245)
    c: Equal(g244,g246)
    c: InternalAlignment(g244,g247)
    c: InternalAlignment(g245,g247)
    c: InternalAlignment(g246,g247)
    c: InternalAlignment(g248,g247)
    c: InternalAlignment(g249,g247)
    c: Block(g229)
    c: Block(g235)
    c: Block(g241)
    c: Block(g247)
    c: Coincident(g250,g235)
    c: Coincident(g250,g229)
    c: Horizontal(g250)
    c: Block(g192)
    c: Weight(g251) = 1
    c: Equal(g251,g252)
    c: Equal(g251,g253)
    c: InternalAlignment(g251,g254)
    c: InternalAlignment(g252,g254)
    c: InternalAlignment(g253,g254)
    c: InternalAlignment(g255,g254)
    c: InternalAlignment(g256,g254)
    c: Weight(g257) = 1
    c: Equal(g257,g258)
    c: Equal(g257,g259)
    c: InternalAlignment(g257,g260)
    c: InternalAlignment(g258,g260)
    c: InternalAlignment(g259,g260)
    c: InternalAlignment(g261,g260)
    c: InternalAlignment(g262,g260)
    c: Block(g254)
    c: Block(g260)
    c: Coincident(g263,g254)
    c: Coincident(g263,g260)
    c: Weight(g264) = 1
    c: Equal(g264,g265)
    c: Equal(g264,g266)
    c: InternalAlignment(g264,g267)
    c: InternalAlignment(g265,g267)
    c: InternalAlignment(g266,g267)
    c: InternalAlignment(g268,g267)
    c: InternalAlignment(g269,g267)
    c: Weight(g270) = 1
    c: Equal(g270,g271)
    c: Equal(g270,g272)
    c: InternalAlignment(g270,g273)
    c: InternalAlignment(g271,g273)
    c: InternalAlignment(g272,g273)
    c: InternalAlignment(g274,g273)
    c: InternalAlignment(g275,g273)
    c: Weight(g276) = 1
    c: Equal(g276,g277)
    c: Equal(g276,g278)
    c: InternalAlignment(g276,g279)
    c: InternalAlignment(g277,g279)
    c: InternalAlignment(g278,g279)
    c: InternalAlignment(g280,g279)
    c: InternalAlignment(g281,g279)
    c: Block(g279)
    c: Block(g273)
    c: Block(g267)
    c: Coincident(g282,g273)
    c: Coincident(g282,g267)
    c: Coincident(g283,g267)
    c: Coincident(g283,g279)
    c: Vertical(g283)
    c: Coincident(g284,g279)
    c: Coincident(g284,g273)
    c: Horizontal(g284)
    c: Weight(g285) = 1
    c: Equal(g285,g286)
    c: InternalAlignment(g285,g287)
    c: InternalAlignment(g286,g287)
    c: InternalAlignment(g288,g287)
    c: InternalAlignment(g289,g287)
    c: Weight(g290) = 1
    c: InternalAlignment(g291,g293)
    c: InternalAlignment(g292,g293)
    c: InternalAlignment(g294,g293)
    c: InternalAlignment(g295,g293)
    c: Weight(g296) = 1
    c: Equal(g296,g297)
    c: Equal(g296,g298)
    c: InternalAlignment(g296,g299)
    c: InternalAlignment(g297,g299)
    c: InternalAlignment(g298,g299)
    c: InternalAlignment(g300,g299)
    c: InternalAlignment(g301,g299)
    c: Equal(g302,g303)
    c: Equal(g302,g304)
    c: InternalAlignment(g302,g305)
    c: InternalAlignment(g303,g305)
    c: InternalAlignment(g304,g305)
    c: InternalAlignment(g306,g305)
    c: InternalAlignment(g307,g305)
    c: Block(g293)
    c: Block(g299)
    c: Block(g305)
    c: Block(g287)
    c: Coincident(g308,g287)
    c: Coincident(g308,g293)
    c: Horizontal(g308)
    c: Coincident(g309,g293)
    c: Coincident(g309,g299)
    c: Vertical(g309)
    c: Coincident(g310,g299)
    c: Coincident(g310,g305)
    c: Horizontal(g310)
    c: Coincident(g311,g305)
    c: Coincident(g311,g287)
    c: Weight(g312) = 1
    c: Equal(g312,g313)
    c: Equal(g312,g314)
    c: InternalAlignment(g312,g315)
    c: InternalAlignment(g313,g315)
    c: InternalAlignment(g314,g315)
    c: InternalAlignment(g316,g315)
    c: InternalAlignment(g317,g315)
    c: Weight(g318) = 1
    c: Equal(g318,g319)
    c: Equal(g318,g320)
    c: InternalAlignment(g318,g321)
    c: InternalAlignment(g319,g321)
    c: InternalAlignment(g320,g321)
    c: InternalAlignment(g322,g321)
    c: InternalAlignment(g323,g321)
    c: Weight(g324) = 1
    c: Equal(g324,g325)
    c: Equal(g324,g326)
    c: InternalAlignment(g324,g327)
    c: InternalAlignment(g325,g327)
    c: InternalAlignment(g326,g327)
    c: InternalAlignment(g328,g327)
    c: InternalAlignment(g329,g327)
    c: Block(g327)
    c: Block(g321)
    c: Block(g315)
    c: Coincident(g330,g327)
    c: Coincident(g330,g321)
    c: Horizontal(g330)
    c: Coincident(g331,g321)
    c: Coincident(g331,g315)
    c: Vertical(g331)
    c: Coincident(g332,g315)
    c: Coincident(g332,g327)
    c: InternalAlignment(g333,g334)
    c: InternalAlignment(g335,g334)
    c: InternalAlignment(g336,g334)
    c: Block(g334)
    c: Equal(g337,g338)
    c: Equal(g337,g339)
    c: InternalAlignment(g337,g340)
    c: InternalAlignment(g338,g340)
    c: InternalAlignment(g339,g340)
    c: InternalAlignment(g341,g340)
    c: InternalAlignment(g342,g340)
    c: Block(g340)
    c: Coincident(g343,g334)
    c: Horizontal(g343)
    c: Block(g343)
    c: Coincident(g344,g334)
    c: Coincident(g344,g260)
    c: Vertical(g344)
    c: Coincident(g345,g340)
    c: Coincident(g345,g254)
    c: Vertical(g345)
    c: Coincident(g347,g5)
    c: Coincident(g348,g5)
    c: Block(g346)
    c: Block(g5)
    c: Block(g348)
    c: Block(g347)
    c: Distance(g344) = 119.89
FEATURE [Sketcher::SketchObject] Sketch001
  FullyConstrained = true
  MapMode = 4
  Placement = pos=(0,0,0) rot=(0.57735,0.57735,0.57735;2.0944rad)
  Support = -> [Sketch]
  sketch-geometry (46):
    g0: BSplineCurve PolesCount=3 KnotsCount=2 Degree=2 IsPeriodic=0
    g1: ArcOfCircle CenterX=73.1223 CenterY=-32.291 CenterZ=0 NormalX=0 NormalY=0 NormalZ=1 AngleXU=0 Radius=13 StartAngle=5.92268 EndAngle=9.06428
    g2: ArcOfCircle CenterX=66.7816 CenterY=-49.1439 CenterZ=0 NormalX=0 NormalY=0 NormalZ=1 AngleXU=0 Radius=13 StartAngle=2.78068 EndAngle=5.92131
    g3: ArcOfCircle CenterX=55.9263 CenterY=-78.1807 CenterZ=0 NormalX=0 NormalY=0 NormalZ=1 AngleXU=0 Radius=13 StartAngle=5.92268 EndAngle=9.06428
    g4: ArcOfCircle CenterX=49.5884 CenterY=-95.0342 CenterZ=0 NormalX=0 NormalY=0 NormalZ=1 AngleXU=0 Radius=13 StartAngle=2.78068 EndAngle=5.92131
    g5: ArcOfCircle CenterX=38.7206 CenterY=-124.067 CenterZ=0 NormalX=0 NormalY=0 NormalZ=1 AngleXU=0 Radius=13 StartAngle=5.92268 EndAngle=9.06428
    g6: ArcOfCircle CenterX=32.3875 CenterY=-140.92 CenterZ=0 NormalX=0 NormalY=0 NormalZ=1 AngleXU=0 Radius=13 StartAngle=2.78068 EndAngle=5.92131
    g7: ArcOfCircle CenterX=21.4715 CenterY=-169.934 CenterZ=0 NormalX=0 NormalY=0 NormalZ=1 AngleXU=0 Radius=13 StartAngle=5.92268 EndAngle=9.06428
    g8: ArcOfCircle CenterX=15.1336 CenterY=-186.787 CenterZ=0 NormalX=0 NormalY=0 NormalZ=1 AngleXU=0 Radius=13 StartAngle=2.78068 EndAngle=5.92131
    g9-g12: Circle x4 (B-spline internal-alignment scaffolding for g13; pole/knot coordinates omitted)
    g13: BSplineCurve PolesCount=4 KnotsCount=2 Degree=3 IsPeriodic=0
    g14: GeomPoint X=28.8094 Y=-19.0875 Z=0
    g15: GeomPoint X=47.0443 Y=-50.4712 Z=0
    g16: Circle CenterX=53.5586 CenterY=-23.2695 CenterZ=0 NormalX=0 NormalY=0 NormalZ=1 AngleXU=0 Radius=3.24518
    g17: Circle CenterX=-195.441 CenterY=-127.082 CenterZ=0 NormalX=0 NormalY=0 NormalZ=1 AngleXU=0 Radius=1
    g18: Circle CenterX=-8.24091 CenterY=-197.481 CenterZ=0 NormalX=0 NormalY=0 NormalZ=1 AngleXU=0 Radius=1
    g19: Circle CenterX=12.8789 CenterY=-141.321 CenterZ=0 NormalX=0 NormalY=0 NormalZ=1 AngleXU=0 Radius=1
    g20: BSplineCurve PolesCount=3 KnotsCount=2 Degree=2 IsPeriodic=0
    g21: GeomPoint X=-195.441 Y=-127.082 Z=0
    g22: GeomPoint X=12.8789 Y=-141.321 Z=0
    g23: Circle CenterX=-12.8016 CenterY=-179.036 CenterZ=0 NormalX=0 NormalY=0 NormalZ=1 AngleXU=0 Radius=10.5072
    g24: Circle CenterX=0.933922 CenterY=-166.43 CenterZ=0 NormalX=0 NormalY=0 NormalZ=1 AngleXU=0 Radius=3.26661
    g25: Circle CenterX=-33.5518 CenterY=-176.44 CenterZ=0 NormalX=0 NormalY=0 NormalZ=1 AngleXU=0 Radius=5.64388
    g26: Circle CenterX=-47.2366 CenterY=-173.859 CenterZ=0 NormalX=0 NormalY=0 NormalZ=1 AngleXU=0 Radius=3.01653
    g27: Circle CenterX=-56.2595 CenterY=-171.456 CenterZ=0 NormalX=0 NormalY=0 NormalZ=1 AngleXU=0 Radius=2.12826
    g28: ArcOfCircle CenterX=51.2151 CenterY=-198.473 CenterZ=0 NormalX=0 NormalY=0 NormalZ=1 AngleXU=0 Radius=20 StartAngle=2.78189 EndAngle=4.35269
    g29: LineSegment StartX=32.4951 StartY=-191.433 StartZ=0 EndX=94.6578 EndY=-26.1352 EndZ=0
    g30: LineSegment StartX=43.1192 StartY=-220.001 StartZ=0 EndX=-196.497 EndY=-129.89 EndZ=0
    g31: LineSegment StartX=43.1192 StartY=-220.001 StartZ=0 EndX=44.1752 EndY=-217.193 EndZ=0
    g32: LineSegment StartX=117.223 StartY=-19.0875 StartZ=0 EndX=117.223 EndY=-16.0875 EndZ=0
    g33: LineSegment StartX=117.223 StartY=-16.0875 StartZ=0 EndX=17.2232 EndY=-16.0875 EndZ=0
    g34: LineSegment StartX=17.2232 StartY=-16.0875 StartZ=0 EndX=17.2232 EndY=-19.0875 EndZ=0
    g35: LineSegment StartX=28.8094 StartY=-19.0875 StartZ=0 EndX=17.2232 EndY=-19.0875 EndZ=0
    g36: LineSegment StartX=47.0443 StartY=-50.4712 StartZ=0 EndX=12.8789 EndY=-141.321 EndZ=0
    g37: LineSegment StartX=-195.441 StartY=-127.082 StartZ=0 EndX=-196.497 EndY=-129.89 EndZ=0
    g38: LineSegment StartX=85.2866 StartY=-36.8766 StartZ=0 EndX=78.9396 EndY=-53.7463 EndZ=0
    g39: LineSegment StartX=60.9579 StartY=-27.7053 StartZ=0 EndX=54.6191 EndY=-44.5532 EndZ=0
    g40: LineSegment StartX=68.0907 StartY=-82.7664 StartZ=0 EndX=61.7465 EndY=-99.6365 EndZ=0
    g41: LineSegment StartX=43.7619 StartY=-73.595 StartZ=0 EndX=37.426 EndY=-90.4435 EndZ=0
    g42: LineSegment StartX=50.885 StartY=-128.652 StartZ=0 EndX=44.5456 EndY=-145.522 EndZ=0
    g43: LineSegment StartX=26.5562 StartY=-119.481 StartZ=0 EndX=20.2251 EndY=-136.329 EndZ=0
    g44: LineSegment StartX=9.3071 StartY=-165.349 StartZ=0 EndX=2.97115 EndY=-182.197 EndZ=0
    g45: LineSegment StartX=33.6358 StartY=-174.52 StartZ=0 EndX=27.2917 EndY=-191.39 EndZ=0
  constraints (71):
    c: Block(g0)
    c: Block(g1)
    c: Block(g2)
    c: Block(g4)
    c: Block(g3)
    c: Block(g6)
    c: Block(g5)
    c: Block(g8)
    c: Block(g7)
    c: Weight(g9) = 1
    c: Equal(g9,g10)
    c: Equal(g9,g11)
    c: Equal(g9,g12)
    c: InternalAlignment(g9-g12 -> g13) x4
    c: InternalAlignment(g14,g13)
    c: InternalAlignment(g15,g13)
    c: Block(g16)
    c: Weight(g17) = 1
    c: Equal(g17,g18)
    c: Equal(g17,g19)
    c: InternalAlignment(g17,g20)
    c: InternalAlignment(g18,g20)
    c: InternalAlignment(g19,g20)
    c: InternalAlignment(g21,g20)
    c: InternalAlignment(g22,g20)
    c: Block(g20)
    c: Block(g23)
    c: Block(g24)
    c: Block(g25)
    c: Block(g26)
    c: Block(g27)
    c: Block(g28)
    c: Coincident(g29,g28)
    c: Coincident(g29,g0)
    c: Block(g13)
    c: Coincident(g31,g30)
    c: Coincident(g31,g28)
    c: Block(g31)
    c: Coincident(g32,g0)
    c: Vertical(g32)
    c: Coincident(g33,g32)
    c: Horizontal(g33)
    c: Coincident(g34,g33)
    c: Vertical(g34)
    c: Block(g33)
    c: Coincident(g35,g13)
    c: Coincident(g35,g34)
    c: Horizontal(g35)
    c: Coincident(g36,g13)
    c: Coincident(g36,g20)
    c: Coincident(g37,g20)
    c: Coincident(g37,g30)
    c: Block(g30)
    c: Coincident(g38,g1)
    c: Coincident(g38,g2)
    c: Coincident(g39,g1)
    c: Coincident(g39,g2)
    c: Coincident(g40,g3)
    c: Coincident(g40,g4)
    c: Coincident(g41,g3)
    c: Coincident(g41,g4)
    c: Coincident(g42,g5)
    c: Coincident(g42,g6)
    c: Coincident(g43,g5)
    c: Coincident(g43,g6)
    c: Coincident(g44,g7)
    c: Coincident(g44,g8)
    c: Coincident(g45,g7)
    c: Coincident(g45,g8)
    c: Distance(g30) = 256
    c: Distance(g33) = 100
FEATURE [Part::Extrusion] Extrude002
  Base = -> Sketch001
  Dir = (1,0,0)
  DirMode = 2
  FaceMakerClass = Part::FaceMakerBullseye
  LengthFwd = 8
  LengthRev = 0
  Solid = true
  Symmetric = false
FEATURE [Sketcher::SketchObject] Sketch002
  FullyConstrained = true
  sketch-geometry (20):
    g0: LineSegment StartX=-2.77179 StartY=-200.304 StartZ=0 EndX=5.22821 EndY=-200.304 EndZ=0
    g1: LineSegment StartX=5.22821 StartY=-200.304 StartZ=0 EndX=5.22821 EndY=-197.304 EndZ=0
    g2: LineSegment StartX=-2.77179 StartY=-200.304 StartZ=0 EndX=-2.77179 EndY=-197.304 EndZ=0
    g3: LineSegment StartX=5.22821 StartY=-197.304 StartZ=0 EndX=8.22821 EndY=-197.304 EndZ=0
    g4: LineSegment StartX=-2.77179 StartY=-197.304 StartZ=0 EndX=-5.77179 EndY=-197.304 EndZ=0
    g5: LineSegment StartX=19.2282 StartY=-203.304 StartZ=0 EndX=19.2282 EndY=-206.304 EndZ=0
    g6: LineSegment StartX=-16.7718 StartY=-203.304 StartZ=0 EndX=-16.7718 EndY=-206.304 EndZ=0
    g7: LineSegment StartX=-16.7718 StartY=-206.304 StartZ=0 EndX=19.2282 EndY=-206.304 EndZ=0
    g8: Circle CenterX=-16.7718 CenterY=-203.304 CenterZ=0 NormalX=0 NormalY=0 NormalZ=1 AngleXU=0 Radius=1
    g9: Circle CenterX=-5.77179 CenterY=-203.304 CenterZ=0 NormalX=0 NormalY=0 NormalZ=1 AngleXU=0 Radius=1
    g10: Circle CenterX=-5.77179 CenterY=-197.304 CenterZ=0 NormalX=0 NormalY=0 NormalZ=1 AngleXU=0 Radius=1
    g11: BSplineCurve PolesCount=3 KnotsCount=2 Degree=2 IsPeriodic=0
    g12: GeomPoint X=-16.7718 Y=-203.304 Z=0
    g13: GeomPoint X=-5.77179 Y=-197.304 Z=0
    g14: Circle CenterX=19.2282 CenterY=-203.304 CenterZ=0 NormalX=0 NormalY=0 NormalZ=1 AngleXU=0 Radius=1
    g15: Circle CenterX=8.22821 CenterY=-203.304 CenterZ=0 NormalX=0 NormalY=0 NormalZ=1 AngleXU=0 Radius=1
    g16: Circle CenterX=8.22821 CenterY=-197.304 CenterZ=0 NormalX=0 NormalY=0 NormalZ=1 AngleXU=0 Radius=1
    g17: BSplineCurve PolesCount=3 KnotsCount=2 Degree=2 IsPeriodic=0
    g18: GeomPoint X=19.2282 Y=-203.304 Z=0
    g19: GeomPoint X=8.22821 Y=-197.304 Z=0
  constraints (41):
    c: Horizontal(g0)
    c: Distance(g0) = 8
    c: Coincident(g1,g0)
    c: Vertical(g1)
    c: Distance(g1) = 3
    c: Coincident(g2,g0)
    c: Vertical(g2)
    c: Distance(g2) = 3
    c: Coincident(g3,g1)
    c: Horizontal(g3)
    c: Distance(g3) = 3
    c: Coincident(g4,g2)
    c: Horizontal(g4)
    c: Distance(g4) = 3
    c: Vertical(g5)
    c: Vertical(g6)
    c: Coincident(g7,g6)
    c: Coincident(g7,g5)
    c: Weight(g8) = 1
    c: Equal(g8,g9)
    c: Equal(g8,g10)
    c: Coincident(g11,g4)
    c: InternalAlignment(g8,g11)
    c: InternalAlignment(g9,g11)
    c: InternalAlignment(g10,g11)
    c: InternalAlignment(g12,g11)
    c: InternalAlignment(g13,g11)
    c: Coincident(g17,g5)
    c: Weight(g14) = 1
    c: Equal(g14,g15)
    c: Equal(g14,g16)
    c: Coincident(g17,g3)
    c: InternalAlignment(g14,g17)
    c: InternalAlignment(g15,g17)
    c: InternalAlignment(g16,g17)
    c: InternalAlignment(g18,g17)
    c: InternalAlignment(g19,g17)
    c: Block(g7)
    c: Block(g17)
    c: Block(g11)
    c: Block(g6)
FEATURE [Part::Extrusion] Extrude003
  Base = -> Sketch002
  Dir = (0,0,1)
  DirMode = 2
  FaceMakerClass = Part::FaceMakerBullseye
  LengthFwd = 260
  LengthRev = 0
  Solid = true
  Symmetric = false
FEATURE [Sketcher::SketchObject] Sketch003
  FullyConstrained = false
  sketch-geometry (376):
    g0: LineSegment StartX=-42.9272 StartY=136.221 StartZ=0 EndX=-42.9272 EndY=-103.779 EndZ=0
    g1: LineSegment StartX=407.073 StartY=136.221 StartZ=0 EndX=407.073 EndY=-103.779 EndZ=0
    g2: ArcOfCircle CenterX=-26.9272 CenterY=-83.7794 CenterZ=0 NormalX=0 NormalY=0 NormalZ=1 AngleXU=0 Radius=8 StartAngle=3.14159 EndAngle=6.28319
    g3: ArcOfCircle CenterX=391.073 CenterY=-83.7794 CenterZ=0 NormalX=0 NormalY=0 NormalZ=1 AngleXU=0 Radius=8 StartAngle=3.14159 EndAngle=6.28319
    g4: Circle CenterX=175.022 CenterY=27.0628 CenterZ=0 NormalX=0 NormalY=0 NormalZ=1 AngleXU=0 Radius=1
    g5: Circle CenterX=179.022 CenterY=24.8665 CenterZ=0 NormalX=0 NormalY=0 NormalZ=1 AngleXU=0 Radius=1
    g6: Circle CenterX=179.022 CenterY=27.0628 CenterZ=0 NormalX=0 NormalY=0 NormalZ=1 AngleXU=0 Radius=1
    g7: BSplineCurve PolesCount=3 KnotsCount=2 Degree=2 IsPeriodic=0
    g8: GeomPoint X=175.022 Y=27.0628 Z=0
    g9: GeomPoint X=179.022 Y=27.0628 Z=0
    g10: Circle CenterX=189.124 CenterY=27.0628 CenterZ=0 NormalX=0 NormalY=0 NormalZ=1 AngleXU=0 Radius=1
    g11: Circle CenterX=185.124 CenterY=24.8665 CenterZ=0 NormalX=0 NormalY=0 NormalZ=1 AngleXU=0 Radius=1
    g12: Circle CenterX=185.124 CenterY=27.0628 CenterZ=0 NormalX=0 NormalY=0 NormalZ=1 AngleXU=0 Radius=1
    g13: BSplineCurve PolesCount=3 KnotsCount=2 Degree=2 IsPeriodic=0
    g14: GeomPoint X=189.124 Y=27.0628 Z=0
    g15: GeomPoint X=185.124 Y=27.0628 Z=0
    g16: Circle CenterX=175.022 CenterY=5.37834 CenterZ=0 NormalX=0 NormalY=0 NormalZ=1 AngleXU=0 Radius=1
    g17: Circle CenterX=179.022 CenterY=7.57463 CenterZ=0 NormalX=0 NormalY=0 NormalZ=1 AngleXU=0 Radius=1
    g18: Circle CenterX=179.022 CenterY=5.34704 CenterZ=0 NormalX=0 NormalY=0 NormalZ=1 AngleXU=0 Radius=1
    g19: BSplineCurve PolesCount=3 KnotsCount=2 Degree=2 IsPeriodic=0
    g20: GeomPoint X=175.022 Y=5.37834 Z=0
    g21: GeomPoint X=179.022 Y=5.34704 Z=0
    g22: Circle CenterX=189.124 CenterY=5.37834 CenterZ=0 NormalX=0 NormalY=0 NormalZ=1 AngleXU=0 Radius=1
    g23: Circle CenterX=185.124 CenterY=7.57463 CenterZ=0 NormalX=0 NormalY=0 NormalZ=1 AngleXU=0 Radius=1
    g24: Circle CenterX=185.124 CenterY=5.34704 CenterZ=0 NormalX=0 NormalY=0 NormalZ=1 AngleXU=0 Radius=1
    g25: BSplineCurve PolesCount=3 KnotsCount=2 Degree=2 IsPeriodic=0
    g26: GeomPoint X=189.124 Y=5.37834 Z=0
    g27: GeomPoint X=185.124 Y=5.34704 Z=0
    g28: Circle CenterX=165.871 CenterY=18.1458 CenterZ=0 NormalX=0 NormalY=0 NormalZ=1 AngleXU=0 Radius=1
    g29: Circle CenterX=169.377 CenterY=16.2206 CenterZ=0 NormalX=0 NormalY=0 NormalZ=1 AngleXU=0 Radius=1
    g30: Circle CenterX=165.871 CenterY=14.2954 CenterZ=0 NormalX=0 NormalY=0 NormalZ=1 AngleXU=0 Radius=1
    g31: BSplineCurve PolesCount=3 KnotsCount=2 Degree=2 IsPeriodic=0
    g32: GeomPoint X=165.871 Y=18.1458 Z=0
    g33: GeomPoint X=165.871 Y=14.2954 Z=0
    g34: Circle CenterX=198.275 CenterY=18.1458 CenterZ=0 NormalX=0 NormalY=0 NormalZ=1 AngleXU=0 Radius=1
    g35: Circle CenterX=194.768 CenterY=16.2206 CenterZ=0 NormalX=0 NormalY=0 NormalZ=1 AngleXU=0 Radius=1
    g36: Circle CenterX=198.275 CenterY=14.2954 CenterZ=0 NormalX=0 NormalY=0 NormalZ=1 AngleXU=0 Radius=1
    g37: BSplineCurve PolesCount=3 KnotsCount=2 Degree=2 IsPeriodic=0
    g38: GeomPoint X=198.275 Y=18.1458 Z=0
    g39: GeomPoint X=198.275 Y=14.2954 Z=0
    g40: LineSegment StartX=407.073 StartY=-103.779 StartZ=0 EndX=-42.9272 EndY=-103.779 EndZ=0
    g41: LineSegment StartX=407.073 StartY=136.221 StartZ=0 EndX=-42.9272 EndY=136.221 EndZ=0
    g42: Circle CenterX=125.607 CenterY=54.1951 CenterZ=0 NormalX=0 NormalY=0 NormalZ=1 AngleXU=0 Radius=1
    g43: Circle CenterX=139.632 CenterY=46.4944 CenterZ=0 NormalX=0 NormalY=0 NormalZ=1 AngleXU=0 Radius=1
    g44: Circle CenterX=127.326 CenterY=56.7187 CenterZ=0 NormalX=0 NormalY=0 NormalZ=1 AngleXU=0 Radius=1
    g45: BSplineCurve PolesCount=3 KnotsCount=2 Degree=2 IsPeriodic=0
    g46: GeomPoint X=125.607 Y=54.1951 Z=0
    g47: GeomPoint X=127.326 Y=56.7187 Z=0
    g48: Circle CenterX=236.821 CenterY=56.7187 CenterZ=0 NormalX=0 NormalY=0 NormalZ=1 AngleXU=0 Radius=1
    g49: Circle CenterX=224.513 CenterY=46.4944 CenterZ=0 NormalX=0 NormalY=0 NormalZ=1 AngleXU=0 Radius=1
    g50: Circle CenterX=238.538 CenterY=54.1951 CenterZ=0 NormalX=0 NormalY=0 NormalZ=1 AngleXU=0 Radius=1
    g51: BSplineCurve PolesCount=3 KnotsCount=2 Degree=2 IsPeriodic=0
    g52: GeomPoint X=236.821 Y=56.7187 Z=0
    g53: GeomPoint X=238.538 Y=54.1951 Z=0
    g54: Circle CenterX=238.538 CenterY=-21.7539 CenterZ=0 NormalX=0 NormalY=0 NormalZ=1 AngleXU=0 Radius=1
    g55: Circle CenterX=224.513 CenterY=-14.0532 CenterZ=0 NormalX=0 NormalY=0 NormalZ=1 AngleXU=0 Radius=1
    g56: Circle CenterX=236.821 CenterY=-24.2775 CenterZ=0 NormalX=0 NormalY=0 NormalZ=1 AngleXU=0 Radius=1
    g57: BSplineCurve PolesCount=3 KnotsCount=2 Degree=2 IsPeriodic=0
    g58: GeomPoint X=238.538 Y=-21.7539 Z=0
    g59: GeomPoint X=236.821 Y=-24.2775 Z=0
    g60: Circle CenterX=125.607 CenterY=-21.7539 CenterZ=0 NormalX=0 NormalY=0 NormalZ=1 AngleXU=0 Radius=1
    g61: Circle CenterX=139.632 CenterY=-14.0532 CenterZ=0 NormalX=0 NormalY=0 NormalZ=1 AngleXU=0 Radius=1
    g62: Circle CenterX=127.325 CenterY=-24.2775 CenterZ=0 NormalX=0 NormalY=0 NormalZ=1 AngleXU=0 Radius=1
    g63: BSplineCurve PolesCount=3 KnotsCount=2 Degree=2 IsPeriodic=0
    g64: GeomPoint X=125.607 Y=-21.7539 Z=0
    g65: GeomPoint X=127.325 Y=-24.2775 Z=0
    g66: Circle CenterX=302.996 CenterY=111.695 CenterZ=0 NormalX=0 NormalY=0 NormalZ=1 AngleXU=0 Radius=1
    g67: Circle CenterX=306.073 CenterY=114.251 CenterZ=0 NormalX=0 NormalY=0 NormalZ=1 AngleXU=0 Radius=1
    g68: Circle CenterX=306.073 CenterY=110.251 CenterZ=0 NormalX=0 NormalY=0 NormalZ=1 AngleXU=0 Radius=1
    g69: BSplineCurve PolesCount=3 KnotsCount=2 Degree=2 IsPeriodic=0
    g70: GeomPoint X=302.996 Y=111.695 Z=0
    g71: GeomPoint X=306.073 Y=110.251 Z=0
    g72: Circle CenterX=306.073 CenterY=95.2763 CenterZ=0 NormalX=0 NormalY=0 NormalZ=1 AngleXU=0 Radius=1
    g73: Circle CenterX=306.073 CenterY=91.2763 CenterZ=0 NormalX=0 NormalY=0 NormalZ=1 AngleXU=0 Radius=1
    g74: Circle CenterX=302.567 CenterY=89.3511 CenterZ=0 NormalX=0 NormalY=0 NormalZ=1 AngleXU=0 Radius=1
    g75: BSplineCurve PolesCount=3 KnotsCount=2 Degree=2 IsPeriodic=0
    g76: GeomPoint X=306.073 Y=95.2763 Z=0
    g77: GeomPoint X=302.567 Y=89.3511 Z=0
    g78: LineSegment StartX=306.073 StartY=110.251 StartZ=0 EndX=306.073 EndY=95.2763 EndZ=0
    g79: LineSegment StartX=302.996 StartY=111.695 StartZ=0 EndX=236.821 EndY=56.7187 EndZ=0
    g80: LineSegment StartX=238.538 StartY=54.1951 StartZ=0 EndX=302.567 EndY=89.3511 EndZ=0
    g81: Circle CenterX=61.1496 CenterY=111.695 CenterZ=0 NormalX=0 NormalY=0 NormalZ=1 AngleXU=0 Radius=1
    g82: Circle CenterX=58.0728 CenterY=114.251 CenterZ=0 NormalX=0 NormalY=0 NormalZ=1 AngleXU=0 Radius=1
    g83: Circle CenterX=58.0728 CenterY=110.251 CenterZ=0 NormalX=0 NormalY=0 NormalZ=1 AngleXU=0 Radius=1
    g84: BSplineCurve PolesCount=3 KnotsCount=2 Degree=2 IsPeriodic=0
    g85: GeomPoint X=61.1496 Y=111.695 Z=0
    g86: GeomPoint X=58.0728 Y=110.251 Z=0
    g87: Circle CenterX=61.5791 CenterY=89.3511 CenterZ=0 NormalX=0 NormalY=0 NormalZ=1 AngleXU=0 Radius=1
    g88: Circle CenterX=58.0728 CenterY=91.2763 CenterZ=0 NormalX=0 NormalY=0 NormalZ=1 AngleXU=0 Radius=1
    g89: Circle CenterX=58.0728 CenterY=95.2763 CenterZ=0 NormalX=0 NormalY=0 NormalZ=1 AngleXU=0 Radius=1
    g90: BSplineCurve PolesCount=3 KnotsCount=2 Degree=2 IsPeriodic=0
    g91: GeomPoint X=61.5791 Y=89.3511 Z=0
    g92: GeomPoint X=58.0728 Y=95.2763 Z=0
    g93: LineSegment StartX=58.0728 StartY=110.251 StartZ=0 EndX=58.0728 EndY=95.2763 EndZ=0
    g94: LineSegment StartX=61.1496 StartY=111.695 StartZ=0 EndX=127.326 EndY=56.7187 EndZ=0
    g95: LineSegment StartX=125.607 StartY=54.1951 StartZ=0 EndX=61.5791 EndY=89.3511 EndZ=0
    g96: Circle CenterX=61.5791 CenterY=-56.9099 CenterZ=0 NormalX=0 NormalY=0 NormalZ=1 AngleXU=0 Radius=1
    g97: Circle CenterX=58.0728 CenterY=-58.8351 CenterZ=0 NormalX=0 NormalY=0 NormalZ=1 AngleXU=0 Radius=1
    g98: Circle CenterX=58.0728 CenterY=-62.8351 CenterZ=0 NormalX=0 NormalY=0 NormalZ=1 AngleXU=0 Radius=1
    g99: BSplineCurve PolesCount=3 KnotsCount=2 Degree=2 IsPeriodic=0
    g100: GeomPoint X=61.5791 Y=-56.9099 Z=0
    g101: GeomPoint X=58.0728 Y=-62.8351 Z=0
    g102: Circle CenterX=58.0728 CenterY=-77.8102 CenterZ=0 NormalX=0 NormalY=0 NormalZ=1 AngleXU=0 Radius=1
    g103: Circle CenterX=58.0728 CenterY=-81.8102 CenterZ=0 NormalX=0 NormalY=0 NormalZ=1 AngleXU=0 Radius=1
    g104: Circle CenterX=61.1496 CenterY=-79.2541 CenterZ=0 NormalX=0 NormalY=0 NormalZ=1 AngleXU=0 Radius=1
    g105: BSplineCurve PolesCount=3 KnotsCount=2 Degree=2 IsPeriodic=0
    g106: GeomPoint X=58.0728 Y=-77.8102 Z=0
    g107: GeomPoint X=61.1496 Y=-79.2541 Z=0
    g108: LineSegment StartX=58.0728 StartY=-62.8351 StartZ=0 EndX=58.0728 EndY=-77.8102 EndZ=0
    g109: LineSegment StartX=61.1496 StartY=-79.2541 StartZ=0 EndX=127.325 EndY=-24.2775 EndZ=0
    g110: LineSegment StartX=125.607 StartY=-21.7539 StartZ=0 EndX=61.5791 EndY=-56.9099 EndZ=0
    g111: Circle CenterX=302.567 CenterY=-56.9099 CenterZ=0 NormalX=0 NormalY=0 NormalZ=1 AngleXU=0 Radius=1
    g112: Circle CenterX=306.073 CenterY=-58.8351 CenterZ=0 NormalX=0 NormalY=0 NormalZ=1 AngleXU=0 Radius=1
    g113: Circle CenterX=306.073 CenterY=-62.8351 CenterZ=0 NormalX=0 NormalY=0 NormalZ=1 AngleXU=0 Radius=1
    g114: BSplineCurve PolesCount=3 KnotsCount=2 Degree=2 IsPeriodic=0
    g115: GeomPoint X=302.567 Y=-56.9099 Z=0
    g116: GeomPoint X=306.073 Y=-62.8351 Z=0
    g117: Circle CenterX=302.996 CenterY=-79.2541 CenterZ=0 NormalX=0 NormalY=0 NormalZ=1 AngleXU=0 Radius=1
    g118: Circle CenterX=306.073 CenterY=-81.8102 CenterZ=0 NormalX=0 NormalY=0 NormalZ=1 AngleXU=0 Radius=1
    g119: Circle CenterX=306.073 CenterY=-77.8102 CenterZ=0 NormalX=0 NormalY=0 NormalZ=1 AngleXU=0 Radius=1
    g120: BSplineCurve PolesCount=3 KnotsCount=2 Degree=2 IsPeriodic=0
    g121: GeomPoint X=302.996 Y=-79.2541 Z=0
    g122: GeomPoint X=306.073 Y=-77.8102 Z=0
    g123: LineSegment StartX=306.073 StartY=-62.8351 StartZ=0 EndX=306.073 EndY=-77.8102 EndZ=0
    g124: LineSegment StartX=302.996 StartY=-79.2541 StartZ=0 EndX=236.821 EndY=-24.2775 EndZ=0
    g125: LineSegment StartX=238.538 StartY=-21.7539 StartZ=0 EndX=302.567 EndY=-56.9099 EndZ=0
    g126: Circle CenterX=61.6457 CenterY=-88.8112 CenterZ=0 NormalX=0 NormalY=0 NormalZ=1 AngleXU=0 Radius=1
    g127: Circle CenterX=58.0728 CenterY=-91.7794 CenterZ=0 NormalX=0 NormalY=0 NormalZ=1 AngleXU=0 Radius=1
    g128: Circle CenterX=63.9135 CenterY=-91.7794 CenterZ=0 NormalX=0 NormalY=0 NormalZ=1 AngleXU=0 Radius=1
    g129: BSplineCurve PolesCount=3 KnotsCount=2 Degree=2 IsPeriodic=0
    g130: GeomPoint X=61.6457 Y=-88.8112 Z=0
    g131: GeomPoint X=63.9135 Y=-91.7794 Z=0
    g132: Circle CenterX=179.022 CenterY=-85.8163 CenterZ=0 NormalX=0 NormalY=0 NormalZ=1 AngleXU=0 Radius=1
    g133: Circle CenterX=179.022 CenterY=-91.7794 CenterZ=0 NormalX=0 NormalY=0 NormalZ=1 AngleXU=0 Radius=1
    g134: Circle CenterX=171.895 CenterY=-91.7794 CenterZ=0 NormalX=0 NormalY=0 NormalZ=1 AngleXU=0 Radius=1
    g135: BSplineCurve PolesCount=3 KnotsCount=2 Degree=2 IsPeriodic=0
    g136: GeomPoint X=179.022 Y=-85.8163 Z=0
    g137: GeomPoint X=171.895 Y=-91.7794 Z=0
    g138: Circle CenterX=185.124 CenterY=-86.2028 CenterZ=0 NormalX=0 NormalY=0 NormalZ=1 AngleXU=0 Radius=1
    g139: Circle CenterX=185.124 CenterY=-91.7794 CenterZ=0 NormalX=0 NormalY=0 NormalZ=1 AngleXU=0 Radius=1
    g140: Circle CenterX=191.747 CenterY=-91.7794 CenterZ=0 NormalX=0 NormalY=0 NormalZ=1 AngleXU=0 Radius=1
    g141: BSplineCurve PolesCount=3 KnotsCount=2 Degree=2 IsPeriodic=0
    g142: GeomPoint X=185.124 Y=-86.2028 Z=0
    g143: GeomPoint X=191.747 Y=-91.7794 Z=0
    g144: Circle CenterX=299.888 CenterY=-86.6413 CenterZ=0 NormalX=0 NormalY=0 NormalZ=1 AngleXU=0 Radius=1
    g145: Circle CenterX=306.073 CenterY=-91.7794 CenterZ=0 NormalX=0 NormalY=0 NormalZ=1 AngleXU=0 Radius=1
    g146: Circle CenterX=298.776 CenterY=-91.7794 CenterZ=0 NormalX=0 NormalY=0 NormalZ=1 AngleXU=0 Radius=1
    g147: BSplineCurve PolesCount=3 KnotsCount=2 Degree=2 IsPeriodic=0
    g148: GeomPoint X=299.888 Y=-86.6413 Z=0
    g149: GeomPoint X=298.776 Y=-91.7794 Z=0
    g150: LineSegment StartX=189.124 StartY=5.37834 StartZ=0 EndX=299.888 EndY=-86.6413 EndZ=0
    g151: LineSegment StartX=298.776 StartY=-91.7794 StartZ=0 EndX=191.747 EndY=-91.7794 EndZ=0
    g152: LineSegment StartX=185.124 StartY=-86.2028 StartZ=0 EndX=185.124 EndY=5.34704 EndZ=0
    g153: LineSegment StartX=179.022 StartY=5.34704 StartZ=0 EndX=179.022 EndY=-85.8163 EndZ=0
    g154: LineSegment StartX=171.895 StartY=-91.7794 StartZ=0 EndX=63.9135 EndY=-91.7794 EndZ=0
    g155: LineSegment StartX=61.6457 StartY=-88.8112 StartZ=0 EndX=175.022 EndY=5.37834 EndZ=0
    g156: Circle CenterX=302.073 CenterY=124.221 CenterZ=0 NormalX=0 NormalY=0 NormalZ=1 AngleXU=0 Radius=1
    g157: Circle CenterX=306.073 CenterY=124.221 CenterZ=0 NormalX=0 NormalY=0 NormalZ=1 AngleXU=0 Radius=1
    g158: Circle CenterX=302.996 CenterY=121.665 CenterZ=0 NormalX=0 NormalY=0 NormalZ=1 AngleXU=0 Radius=1
    g159: BSplineCurve PolesCount=3 KnotsCount=2 Degree=2 IsPeriodic=0
    g160: GeomPoint X=302.073 Y=124.221 Z=0
    g161: GeomPoint X=302.996 Y=121.665 Z=0
    g162: Circle CenterX=189.124 CenterY=124.221 CenterZ=0 NormalX=0 NormalY=0 NormalZ=1 AngleXU=0 Radius=1
    g163: Circle CenterX=185.124 CenterY=124.221 CenterZ=0 NormalX=0 NormalY=0 NormalZ=1 AngleXU=0 Radius=1
    g164: Circle CenterX=185.124 CenterY=120.221 CenterZ=0 NormalX=0 NormalY=0 NormalZ=1 AngleXU=0 Radius=1
    g165: BSplineCurve PolesCount=3 KnotsCount=2 Degree=2 IsPeriodic=0
    g166: GeomPoint X=189.124 Y=124.221 Z=0
    g167: GeomPoint X=185.124 Y=120.221 Z=0
    g168: Circle CenterX=175.022 CenterY=124.221 CenterZ=0 NormalX=0 NormalY=0 NormalZ=1 AngleXU=0 Radius=1
    g169: Circle CenterX=179.022 CenterY=124.221 CenterZ=0 NormalX=0 NormalY=0 NormalZ=1 AngleXU=0 Radius=1
    g170: Circle CenterX=179.022 CenterY=120.221 CenterZ=0 NormalX=0 NormalY=0 NormalZ=1 AngleXU=0 Radius=1
    g171: BSplineCurve PolesCount=3 KnotsCount=2 Degree=2 IsPeriodic=0
    g172: GeomPoint X=175.022 Y=124.221 Z=0
    g173: GeomPoint X=179.022 Y=120.221 Z=0
    g174: Circle CenterX=62.0728 CenterY=124.221 CenterZ=0 NormalX=0 NormalY=0 NormalZ=1 AngleXU=0 Radius=1
    g175: Circle CenterX=58.0728 CenterY=124.221 CenterZ=0 NormalX=0 NormalY=0 NormalZ=1 AngleXU=0 Radius=1
    g176: Circle CenterX=61.1496 CenterY=121.665 CenterZ=0 NormalX=0 NormalY=0 NormalZ=1 AngleXU=0 Radius=1
    g177: BSplineCurve PolesCount=3 KnotsCount=2 Degree=2 IsPeriodic=0
    g178: GeomPoint X=62.0728 Y=124.221 Z=0
    g179: GeomPoint X=61.1496 Y=121.665 Z=0
    g180: LineSegment StartX=62.0728 StartY=124.221 StartZ=0 EndX=175.022 EndY=124.221 EndZ=0
    g181: LineSegment StartX=179.022 StartY=120.221 StartZ=0 EndX=179.022 EndY=27.0628 EndZ=0
    g182: LineSegment StartX=185.124 StartY=27.0628 StartZ=0 EndX=185.124 EndY=120.221 EndZ=0
    g183: LineSegment StartX=189.124 StartY=124.221 StartZ=0 EndX=302.073 EndY=124.221 EndZ=0
    g184: LineSegment StartX=302.996 StartY=121.665 StartZ=0 EndX=189.124 EndY=27.0628 EndZ=0
    g185: LineSegment StartX=175.022 StartY=27.0628 StartZ=0 EndX=61.1496 EndY=121.665 EndZ=0
    g186: Circle CenterX=61.5791 CenterY=75.4095 CenterZ=0 NormalX=0 NormalY=0 NormalZ=1 AngleXU=0 Radius=1
    g187: Circle CenterX=58.0728 CenterY=77.3346 CenterZ=0 NormalX=0 NormalY=0 NormalZ=1 AngleXU=0 Radius=1
    g188: Circle CenterX=58.0728 CenterY=73.3346 CenterZ=0 NormalX=0 NormalY=0 NormalZ=1 AngleXU=0 Radius=1
    g189: BSplineCurve PolesCount=3 KnotsCount=2 Degree=2 IsPeriodic=0
    g190: GeomPoint X=61.5791 Y=75.4095 Z=0
    g191: GeomPoint X=58.0728 Y=73.3346 Z=0
    g192: Circle CenterX=58.0728 CenterY=-40.8935 CenterZ=0 NormalX=0 NormalY=0 NormalZ=1 AngleXU=0 Radius=1
    g193: Circle CenterX=58.0728 CenterY=-44.8935 CenterZ=0 NormalX=0 NormalY=0 NormalZ=1 AngleXU=0 Radius=1
    g194: Circle CenterX=61.5791 CenterY=-42.9683 CenterZ=0 NormalX=0 NormalY=0 NormalZ=1 AngleXU=0 Radius=1
    g195: BSplineCurve PolesCount=3 KnotsCount=2 Degree=2 IsPeriodic=0
    g196: GeomPoint X=58.0728 Y=-40.8935 Z=0
    g197: GeomPoint X=61.5791 Y=-42.9683 Z=0
    g198: LineSegment StartX=61.5791 StartY=-42.9683 StartZ=0 EndX=165.871 EndY=14.2954 EndZ=0
    g199: LineSegment StartX=165.871 StartY=18.1458 StartZ=0 EndX=61.5791 EndY=75.4095 EndZ=0
    g200: LineSegment StartX=58.0728 StartY=73.3346 StartZ=0 EndX=58.0728 EndY=-40.8935 EndZ=0
    g201: Circle CenterX=302.567 CenterY=-42.9683 CenterZ=0 NormalX=0 NormalY=0 NormalZ=1 AngleXU=0 Radius=1
    g202: Circle CenterX=306.073 CenterY=-44.8935 CenterZ=0 NormalX=0 NormalY=0 NormalZ=1 AngleXU=0 Radius=1
    g203: Circle CenterX=306.073 CenterY=-40.8935 CenterZ=0 NormalX=0 NormalY=0 NormalZ=1 AngleXU=0 Radius=1
    g204: BSplineCurve PolesCount=3 KnotsCount=2 Degree=2 IsPeriodic=0
    g205: GeomPoint X=302.567 Y=-42.9683 Z=0
    g206: GeomPoint X=306.073 Y=-40.8935 Z=0
    g207: Circle CenterX=306.073 CenterY=73.3346 CenterZ=0 NormalX=0 NormalY=0 NormalZ=1 AngleXU=0 Radius=1
    g208: Circle CenterX=306.073 CenterY=77.3346 CenterZ=0 NormalX=0 NormalY=0 NormalZ=1 AngleXU=0 Radius=1
    g209: Circle CenterX=302.567 CenterY=75.4095 CenterZ=0 NormalX=0 NormalY=0 NormalZ=1 AngleXU=0 Radius=1
    g210: BSplineCurve PolesCount=3 KnotsCount=2 Degree=2 IsPeriodic=0
    g211: GeomPoint X=306.073 Y=73.3346 Z=0
    g212: GeomPoint X=302.567 Y=75.4095 Z=0
    g213: LineSegment StartX=302.567 StartY=-42.9683 StartZ=0 EndX=198.275 EndY=14.2954 EndZ=0
    g214: LineSegment StartX=198.275 StartY=18.1458 StartZ=0 EndX=302.567 EndY=75.4095 EndZ=0
    g215: LineSegment StartX=306.073 StartY=73.3346 StartZ=0 EndX=306.073 EndY=-40.8935 EndZ=0
    g216: LineSegment StartX=322.073 StartY=105.865 StartZ=0 EndX=328.643 EndY=105.865 EndZ=0
    g217: LineSegment StartX=318.073 StartY=120.221 StartZ=0 EndX=318.073 EndY=109.865 EndZ=0
    g218: LineSegment StartX=336.157 StartY=107.779 StartZ=0 EndX=362.567 EndY=122.294 EndZ=0
    g219: Circle CenterX=362.073 CenterY=124.221 CenterZ=0 NormalX=0 NormalY=0 NormalZ=1 AngleXU=0 Radius=1
    g220: Circle CenterX=366.073 CenterY=124.221 CenterZ=0 NormalX=0 NormalY=0 NormalZ=1 AngleXU=0 Radius=1
    g221: Circle CenterX=362.567 CenterY=122.294 CenterZ=0 NormalX=0 NormalY=0 NormalZ=1 AngleXU=0 Radius=1
    g222: BSplineCurve PolesCount=3 KnotsCount=2 Degree=2 IsPeriodic=0
    g223: GeomPoint X=362.073 Y=124.221 Z=0
    g224: GeomPoint X=362.567 Y=122.294 Z=0
    g225: Circle CenterX=322.073 CenterY=124.221 CenterZ=0 NormalX=0 NormalY=0 NormalZ=1 AngleXU=0 Radius=1
    g226: Circle CenterX=318.073 CenterY=124.221 CenterZ=0 NormalX=0 NormalY=0 NormalZ=1 AngleXU=0 Radius=1
    g227: Circle CenterX=318.073 CenterY=120.221 CenterZ=0 NormalX=0 NormalY=0 NormalZ=1 AngleXU=0 Radius=1
    g228: BSplineCurve PolesCount=3 KnotsCount=2 Degree=2 IsPeriodic=0
    g229: GeomPoint X=322.073 Y=124.221 Z=0
    g230: GeomPoint X=318.073 Y=120.221 Z=0
    g231: Circle CenterX=322.073 CenterY=105.865 CenterZ=0 NormalX=0 NormalY=0 NormalZ=1 AngleXU=0 Radius=1
    g232: Circle CenterX=318.073 CenterY=105.865 CenterZ=0 NormalX=0 NormalY=0 NormalZ=1 AngleXU=0 Radius=1
    g233: Circle CenterX=318.073 CenterY=109.865 CenterZ=0 NormalX=0 NormalY=0 NormalZ=1 AngleXU=0 Radius=1
    g234: BSplineCurve PolesCount=3 KnotsCount=2 Degree=2 IsPeriodic=0
    g235: GeomPoint X=322.073 Y=105.865 Z=0
    g236: GeomPoint X=318.073 Y=109.865 Z=0
    g237: Circle CenterX=336.157 CenterY=107.779 CenterZ=0 NormalX=0 NormalY=0 NormalZ=1 AngleXU=0 Radius=1
    g238: Circle CenterX=332.651 CenterY=105.853 CenterZ=0 NormalX=0 NormalY=0 NormalZ=1 AngleXU=0 Radius=1
    g239: Circle CenterX=328.643 CenterY=105.865 CenterZ=0 NormalX=0 NormalY=0 NormalZ=1 AngleXU=0 Radius=1
    g240: BSplineCurve PolesCount=3 KnotsCount=2 Degree=2 IsPeriodic=0
    g241: GeomPoint X=336.157 Y=107.779 Z=0
    g242: GeomPoint X=328.643 Y=105.865 Z=0
    g243: LineSegment StartX=322.073 StartY=124.221 StartZ=0 EndX=362.073 EndY=124.221 EndZ=0
    g244: Circle CenterX=371.567 CenterY=-80.8644 CenterZ=0 NormalX=0 NormalY=0 NormalZ=1 AngleXU=0 Radius=1
    g245: Circle CenterX=375.073 CenterY=-82.7896 CenterZ=0 NormalX=0 NormalY=0 NormalZ=1 AngleXU=0 Radius=1
    g246: Circle CenterX=375.073 CenterY=-78.7896 CenterZ=0 NormalX=0 NormalY=0 NormalZ=1 AngleXU=0 Radius=1
    g247: BSplineCurve PolesCount=3 KnotsCount=2 Degree=2 IsPeriodic=0
    g248: GeomPoint X=371.567 Y=-80.8644 Z=0
    g249: GeomPoint X=375.073 Y=-78.7896 Z=0
    g250: Circle CenterX=321.579 CenterY=-53.4075 CenterZ=0 NormalX=0 NormalY=0 NormalZ=1 AngleXU=0 Radius=1
    g251: Circle CenterX=318.073 CenterY=-51.4823 CenterZ=0 NormalX=0 NormalY=0 NormalZ=1 AngleXU=0 Radius=1
    g252: Circle CenterX=318.073 CenterY=-47.4805 CenterZ=0 NormalX=0 NormalY=0 NormalZ=1 AngleXU=0 Radius=1
    g253: BSplineCurve PolesCount=3 KnotsCount=2 Degree=2 IsPeriodic=0
    g254: GeomPoint X=321.579 Y=-53.4075 Z=0
    g255: GeomPoint X=318.073 Y=-47.4805 Z=0
    g256: LineSegment StartX=371.567 StartY=-80.8644 StartZ=0 EndX=321.579 EndY=-53.4075 EndZ=0
    g257: Circle CenterX=321.579 CenterY=-67.3492 CenterZ=0 NormalX=0 NormalY=0 NormalZ=1 AngleXU=0 Radius=1
    g258: Circle CenterX=318.073 CenterY=-65.424 CenterZ=0 NormalX=0 NormalY=0 NormalZ=1 AngleXU=0 Radius=1
    g259: Circle CenterX=318.073 CenterY=-69.424 CenterZ=0 NormalX=0 NormalY=0 NormalZ=1 AngleXU=0 Radius=1
    g260: BSplineCurve PolesCount=3 KnotsCount=2 Degree=2 IsPeriodic=0
    g261: GeomPoint X=321.579 Y=-67.3492 Z=0
    g262: GeomPoint X=318.073 Y=-69.424 Z=0
    g263: Circle CenterX=362.567 CenterY=-89.8542 CenterZ=0 NormalX=0 NormalY=0 NormalZ=1 AngleXU=0 Radius=1
    g264: Circle CenterX=366.073 CenterY=-91.7794 CenterZ=0 NormalX=0 NormalY=0 NormalZ=1 AngleXU=0 Radius=1
    g265: Circle CenterX=362.073 CenterY=-91.7794 CenterZ=0 NormalX=0 NormalY=0 NormalZ=1 AngleXU=0 Radius=1
    g266: BSplineCurve PolesCount=3 KnotsCount=2 Degree=2 IsPeriodic=0
    g267: GeomPoint X=362.567 Y=-89.8542 Z=0
    g268: GeomPoint X=362.073 Y=-91.7794 Z=0
    g269: Circle CenterX=322.073 CenterY=-91.7794 CenterZ=0 NormalX=0 NormalY=0 NormalZ=1 AngleXU=0 Radius=1
    g270: Circle CenterX=318.073 CenterY=-91.7794 CenterZ=0 NormalX=0 NormalY=0 NormalZ=1 AngleXU=0 Radius=1
    g271: Circle CenterX=318.073 CenterY=-87.7794 CenterZ=0 NormalX=0 NormalY=0 NormalZ=1 AngleXU=0 Radius=1
    g272: BSplineCurve PolesCount=3 KnotsCount=2 Degree=2 IsPeriodic=0
    g273: GeomPoint X=322.073 Y=-91.7794 Z=0
    g274: GeomPoint X=318.073 Y=-87.7794 Z=0
    g275: LineSegment StartX=362.567 StartY=-89.8542 StartZ=0 EndX=321.579 EndY=-67.3492 EndZ=0
    g276: LineSegment StartX=318.073 StartY=-69.424 StartZ=0 EndX=318.073 EndY=-87.7794 EndZ=0
    g277: LineSegment StartX=322.073 StartY=-91.7794 StartZ=0 EndX=362.073 EndY=-91.7794 EndZ=0
    g278: Circle CenterX=2.07281 CenterY=124.221 CenterZ=0 NormalX=0 NormalY=0 NormalZ=1 AngleXU=0 Radius=1
    g279: Circle CenterX=1.57905 CenterY=122.295 CenterZ=0 NormalX=0 NormalY=0 NormalZ=1 AngleXU=0 Radius=1
    g280: BSplineCurve PolesCount=3 KnotsCount=2 Degree=2 IsPeriodic=0
    g281: GeomPoint X=2.07281 Y=124.221 Z=0
    g282: GeomPoint X=1.57905 Y=122.295 Z=0
    g283: Circle CenterX=42.0728 CenterY=124.221 CenterZ=0 NormalX=0 NormalY=0 NormalZ=1 AngleXU=0 Radius=1
    g284: Circle CenterX=46.0728 CenterY=124.221 CenterZ=0 NormalX=0 NormalY=0 NormalZ=1 AngleXU=0 Radius=1
    g285: Circle CenterX=46.0728 CenterY=120.221 CenterZ=0 NormalX=0 NormalY=0 NormalZ=1 AngleXU=0 Radius=1
    g286: BSplineCurve PolesCount=3 KnotsCount=2 Degree=2 IsPeriodic=0
    g287: GeomPoint X=42.0728 Y=124.221 Z=0
    g288: GeomPoint X=46.0728 Y=120.221 Z=0
    g289: Circle CenterX=46.0728 CenterY=109.865 CenterZ=0 NormalX=0 NormalY=0 NormalZ=1 AngleXU=0 Radius=1
    g290: Circle CenterX=46.0728 CenterY=105.865 CenterZ=0 NormalX=0 NormalY=0 NormalZ=1 AngleXU=0 Radius=1
    g291: Circle CenterX=42.0728 CenterY=105.865 CenterZ=0 NormalX=0 NormalY=0 NormalZ=1 AngleXU=0 Radius=1
    g292: BSplineCurve PolesCount=3 KnotsCount=2 Degree=2 IsPeriodic=0
    g293: GeomPoint X=46.0728 Y=109.865 Z=0
    g294: GeomPoint X=42.0728 Y=105.865 Z=0
    g295: Circle CenterX=35.5028 CenterY=105.865 CenterZ=0 NormalX=0 NormalY=0 NormalZ=1 AngleXU=0 Radius=1
    g296: Circle CenterX=31.5028 CenterY=105.865 CenterZ=0 NormalX=0 NormalY=0 NormalZ=1 AngleXU=0 Radius=1
    g297: Circle CenterX=27.9965 CenterY=107.79 CenterZ=0 NormalX=0 NormalY=0 NormalZ=1 AngleXU=0 Radius=1
    g298: BSplineCurve PolesCount=3 KnotsCount=2 Degree=2 IsPeriodic=0
    g299: GeomPoint X=35.5028 Y=105.865 Z=0
    g300: GeomPoint X=27.9965 Y=107.79 Z=0
    g301: LineSegment StartX=2.07281 StartY=124.221 StartZ=0 EndX=42.0728 EndY=124.221 EndZ=0
    g302: LineSegment StartX=46.0728 StartY=120.221 StartZ=0 EndX=46.0728 EndY=109.865 EndZ=0
    g303: LineSegment StartX=42.0728 StartY=105.865 StartZ=0 EndX=35.5028 EndY=105.865 EndZ=0
    g304: LineSegment StartX=27.9965 StartY=107.79 StartZ=0 EndX=1.57905 EndY=122.295 EndZ=0
    g305: Circle CenterX=42.5666 CenterY=-67.3492 CenterZ=0 NormalX=0 NormalY=0 NormalZ=1 AngleXU=0 Radius=1
    g306: Circle CenterX=46.0728 CenterY=-65.424 CenterZ=0 NormalX=0 NormalY=0 NormalZ=1 AngleXU=0 Radius=1
    g307: Circle CenterX=46.0728 CenterY=-69.424 CenterZ=0 NormalX=0 NormalY=0 NormalZ=1 AngleXU=0 Radius=1
    g308: BSplineCurve PolesCount=3 KnotsCount=2 Degree=2 IsPeriodic=0
    g309: GeomPoint X=42.5666 Y=-67.3492 Z=0
    g310: GeomPoint X=46.0728 Y=-69.424 Z=0
    g311: Circle CenterX=46.0728 CenterY=-87.7794 CenterZ=0 NormalX=0 NormalY=0 NormalZ=1 AngleXU=0 Radius=1
    g312: Circle CenterX=46.0728 CenterY=-91.7794 CenterZ=0 NormalX=0 NormalY=0 NormalZ=1 AngleXU=0 Radius=1
    g313: Circle CenterX=42.0728 CenterY=-91.7794 CenterZ=0 NormalX=0 NormalY=0 NormalZ=1 AngleXU=0 Radius=1
    g314: BSplineCurve PolesCount=3 KnotsCount=2 Degree=2 IsPeriodic=0
    g315: GeomPoint X=46.0728 Y=-87.7794 Z=0
    g316: GeomPoint X=42.0728 Y=-91.7794 Z=0
    g317: Circle CenterX=2.07281 CenterY=-91.7794 CenterZ=0 NormalX=0 NormalY=0 NormalZ=1 AngleXU=0 Radius=1
    g318: Circle CenterX=-1.92719 CenterY=-91.7794 CenterZ=0 NormalX=0 NormalY=0 NormalZ=1 AngleXU=0 Radius=1
    g319: Circle CenterX=1.57905 CenterY=-89.8542 CenterZ=0 NormalX=0 NormalY=0 NormalZ=1 AngleXU=0 Radius=1
    g320: BSplineCurve PolesCount=3 KnotsCount=2 Degree=2 IsPeriodic=0
    g321: GeomPoint X=2.07281 Y=-91.7794 Z=0
    g322: GeomPoint X=1.57905 Y=-89.8542 Z=0
    g323: LineSegment StartX=2.07281 StartY=-91.7794 StartZ=0 EndX=42.0728 EndY=-91.7794 EndZ=0
    g324: LineSegment StartX=46.0728 StartY=-87.7794 StartZ=0 EndX=46.0728 EndY=-69.424 EndZ=0
    g325: LineSegment StartX=42.5666 StartY=-67.3492 StartZ=0 EndX=1.57905 EndY=-89.8542 EndZ=0
    g326: Circle CenterX=322.073 CenterY=76.4095 CenterZ=0 NormalX=0 NormalY=0 NormalZ=1 AngleXU=0 Radius=4
    g327: BSplineCurve PolesCount=3 KnotsCount=2 Degree=2 IsPeriodic=0
    g328: GeomPoint X=318.073 Y=72.4095 Z=0
    g329: GeomPoint X=322.073 Y=76.4095 Z=0
    g330: Circle CenterX=375.073 CenterY=72.4095 CenterZ=0 NormalX=0 NormalY=0 NormalZ=1 AngleXU=0 Radius=1
    g331: Circle CenterX=375.073 CenterY=76.4095 CenterZ=0 NormalX=0 NormalY=0 NormalZ=1 AngleXU=0 Radius=1
    g332: Circle CenterX=371.073 CenterY=76.4095 CenterZ=0 NormalX=0 NormalY=0 NormalZ=1 AngleXU=0 Radius=1
    g333: BSplineCurve PolesCount=3 KnotsCount=2 Degree=2 IsPeriodic=0
    g334: GeomPoint X=375.073 Y=72.4095 Z=0
    g335: GeomPoint X=371.073 Y=76.4095 Z=0
    g336: LineSegment StartX=322.073 StartY=76.4095 StartZ=0 EndX=371.073 EndY=76.4095 EndZ=0
    g337: LineSegment StartX=318.073 StartY=72.4095 StartZ=0 EndX=318.073 EndY=-47.4805 EndZ=0
    g338: LineSegment StartX=375.073 StartY=72.4095 StartZ=0 EndX=375.073 EndY=-78.7896 EndZ=0
    g339: ArcOfCircle CenterX=-26.9272 CenterY=22.1087 CenterZ=0 NormalX=0 NormalY=0 NormalZ=1 AngleXU=0 Radius=4 StartAngle=5e-16 EndAngle=3.14159
    g340: LineSegment StartX=-22.9272 StartY=22.1087 StartZ=0 EndX=-18.9272 EndY=-83.7794 EndZ=0
    g341: LineSegment StartX=-34.9272 StartY=-83.7794 StartZ=0 EndX=-30.9272 EndY=22.1087 EndZ=0
    g342: ArcOfCircle CenterX=391.073 CenterY=22.1087 CenterZ=0 NormalX=0 NormalY=0 NormalZ=1 AngleXU=0 Radius=4 StartAngle=0 EndAngle=3.14159
    g343: LineSegment StartX=387.073 StartY=22.1087 StartZ=0 EndX=383.073 EndY=-83.7794 EndZ=0
    g344: LineSegment StartX=395.073 StartY=22.1087 StartZ=0 EndX=399.073 EndY=-83.7794 EndZ=0
    g345: Circle CenterX=-10.9272 CenterY=-78.7794 CenterZ=0 NormalX=0 NormalY=0 NormalZ=1 AngleXU=0 Radius=1
    g346: Circle CenterX=-10.9272 CenterY=-82.7794 CenterZ=0 NormalX=0 NormalY=0 NormalZ=1 AngleXU=0 Radius=1
    g347: Circle CenterX=-7.42095 CenterY=-80.8542 CenterZ=0 NormalX=0 NormalY=0 NormalZ=1 AngleXU=0 Radius=1
    g348: BSplineCurve PolesCount=3 KnotsCount=2 Degree=2 IsPeriodic=0
    g349: GeomPoint X=-10.9272 Y=-78.7794 Z=0
    g350: GeomPoint X=-7.42095 Y=-80.8542 Z=0
    g351: Circle CenterX=42.5666 CenterY=-53.4075 CenterZ=0 NormalX=0 NormalY=0 NormalZ=1 AngleXU=0 Radius=1
    g352: Circle CenterX=46.0728 CenterY=-51.4823 CenterZ=0 NormalX=0 NormalY=0 NormalZ=1 AngleXU=0 Radius=1
    g353: Circle CenterX=46.0728 CenterY=-47.4823 CenterZ=0 NormalX=0 NormalY=0 NormalZ=1 AngleXU=0 Radius=1
    g354: BSplineCurve PolesCount=3 KnotsCount=2 Degree=2 IsPeriodic=0
    g355: GeomPoint X=42.5666 Y=-53.4075 Z=0
    g356: GeomPoint X=46.0728 Y=-47.4823 Z=0
    g357: Circle CenterX=46.0728 CenterY=72.4095 CenterZ=0 NormalX=0 NormalY=0 NormalZ=1 AngleXU=0 Radius=1
    g358: Circle CenterX=46.0728 CenterY=76.4095 CenterZ=0 NormalX=0 NormalY=0 NormalZ=1 AngleXU=0 Radius=1
    g359: Circle CenterX=42.0728 CenterY=76.4095 CenterZ=0 NormalX=0 NormalY=0 NormalZ=1 AngleXU=0 Radius=1
    g360: BSplineCurve PolesCount=3 KnotsCount=2 Degree=2 IsPeriodic=0
    g361: GeomPoint X=46.0728 Y=72.4095 Z=0
    g362: GeomPoint X=42.0728 Y=76.4095 Z=0
    g363: Circle CenterX=-6.92718 CenterY=76.4095 CenterZ=0 NormalX=0 NormalY=0 NormalZ=1 AngleXU=0 Radius=1
    g364: Circle CenterX=-10.9272 CenterY=76.4095 CenterZ=0 NormalX=0 NormalY=0 NormalZ=1 AngleXU=0 Radius=1
    g365: Circle CenterX=-10.9272 CenterY=72.4095 CenterZ=0 NormalX=0 NormalY=0 NormalZ=1 AngleXU=0 Radius=1
    g366: BSplineCurve PolesCount=3 KnotsCount=2 Degree=2 IsPeriodic=0
    g367: GeomPoint X=-6.92718 Y=76.4095 Z=0
    g368: GeomPoint X=-10.9272 Y=72.4095 Z=0
    g369: LineSegment StartX=-10.9272 StartY=72.4095 StartZ=0 EndX=-10.9272 EndY=-78.7794 EndZ=0
    g370: LineSegment StartX=-7.42095 StartY=-80.8542 StartZ=0 EndX=42.5666 EndY=-53.4075 EndZ=0
    g371: LineSegment StartX=46.0728 StartY=-47.4823 StartZ=0 EndX=46.0728 EndY=72.4095 EndZ=0
    g372: LineSegment StartX=42.0728 StartY=76.4095 StartZ=0 EndX=-6.92719 EndY=76.4095 EndZ=0
    g373: LineSegment StartX=182.072 StartY=136.221 StartZ=0 EndX=182.072 EndY=137.404 EndZ=0
    g374: LineSegment StartX=193.56 StartY=140.32 StartZ=0 EndX=243.56 EndY=140.32 EndZ=0
    g375: LineSegment StartX=136.937 StartY=142.44 StartZ=0 EndX=186.937 EndY=142.44 EndZ=0
  constraints (619):
    c: Vertical(g0)
    c: Vertical(g1)
    c: Block(g1)
    c: Block(g0)
    c: Weight(g4) = 1
    c: Equal(g4,g5)
    c: Equal(g4,g6)
    c: InternalAlignment(g4,g7)
    c: InternalAlignment(g5,g7)
    c: InternalAlignment(g6,g7)
    c: InternalAlignment(g8,g7)
    c: InternalAlignment(g9,g7)
    c: Weight(g10) = 1
    c: Equal(g10,g11)
    c: Equal(g10,g12)
    c: InternalAlignment(g10,g13)
    c: InternalAlignment(g11,g13)
    c: InternalAlignment(g12,g13)
    c: InternalAlignment(g14,g13)
    c: InternalAlignment(g15,g13)
    c: Block(g13)
    c: Block(g7)
    c: Weight(g16) = 1
    c: Equal(g16,g17)
    c: Equal(g16,g18)
    c: InternalAlignment(g16,g19)
    c: InternalAlignment(g17,g19)
    c: InternalAlignment(g18,g19)
    c: InternalAlignment(g20,g19)
    c: InternalAlignment(g21,g19)
    c: Weight(g22) = 1
    c: Equal(g22,g23)
    c: Equal(g22,g24)
    c: InternalAlignment(g22,g25)
    c: InternalAlignment(g23,g25)
    c: InternalAlignment(g24,g25)
    c: InternalAlignment(g26,g25)
    c: InternalAlignment(g27,g25)
    c: Block(g25)
    c: Block(g19)
    c: Weight(g28) = 1
    c: Equal(g28,g29)
    c: Equal(g28,g30)
    c: InternalAlignment(g28,g31)
    c: InternalAlignment(g29,g31)
    c: InternalAlignment(g30,g31)
    c: InternalAlignment(g32,g31)
    c: InternalAlignment(g33,g31)
    c: Weight(g34) = 1
    c: Equal(g34,g35)
    c: Equal(g34,g36)
    c: InternalAlignment(g34,g37)
    c: InternalAlignment(g35,g37)
    c: InternalAlignment(g36,g37)
    c: InternalAlignment(g38,g37)
    c: InternalAlignment(g39,g37)
    c: Block(g31)
    c: Block(g37)
    c: Coincident(g40,g1)
    c: Coincident(g40,g0)
    c: Horizontal(g40)
    c: Distance(g40) = 450
    c: Coincident(g41,g1)
    c: Coincident(g41,g0)
    c: Horizontal(g41)
    c: Weight(g42) = 1
    c: Equal(g42,g43)
    c: Equal(g42,g44)
    c: InternalAlignment(g42,g45)
    c: InternalAlignment(g43,g45)
    c: InternalAlignment(g44,g45)
    c: InternalAlignment(g46,g45)
    c: InternalAlignment(g47,g45)
    c: Block(g45)
    c: Weight(g48) = 1
    c: Equal(g48,g49)
    c: Equal(g48,g50)
    c: InternalAlignment(g48,g51)
    c: InternalAlignment(g49,g51)
    c: InternalAlignment(g50,g51)
    c: InternalAlignment(g52,g51)
    c: InternalAlignment(g53,g51)
    c: Block(g51)
    c: Weight(g54) = 1
    c: Equal(g54,g55)
    c: Equal(g54,g56)
    c: InternalAlignment(g54,g57)
    c: InternalAlignment(g55,g57)
    c: InternalAlignment(g56,g57)
    c: InternalAlignment(g58,g57)
    c: InternalAlignment(g59,g57)
    c: Block(g57)
    c: Weight(g60) = 1
    c: Equal(g60,g61)
    c: Equal(g60,g62)
    c: InternalAlignment(g60,g63)
    c: InternalAlignment(g61,g63)
    c: InternalAlignment(g62,g63)
    c: InternalAlignment(g64,g63)
    c: InternalAlignment(g65,g63)
    c: Block(g63)
    c: Weight(g66) = 1
    c: Equal(g66,g67)
    c: Equal(g66,g68)
    c: InternalAlignment(g66,g69)
    c: InternalAlignment(g67,g69)
    c: InternalAlignment(g68,g69)
    c: InternalAlignment(g70,g69)
    c: InternalAlignment(g71,g69)
    c: Weight(g72) = 1
    c: Equal(g72,g73)
    c: Equal(g72,g74)
    c: InternalAlignment(g72,g75)
    c: InternalAlignment(g73,g75)
    c: InternalAlignment(g74,g75)
    c: InternalAlignment(g76,g75)
    c: InternalAlignment(g77,g75)
    c: Block(g69)
    c: Block(g75)
    c: Coincident(g78,g69)
    c: Coincident(g78,g75)
    c: Vertical(g78)
    c: Coincident(g79,g69)
    c: Coincident(g79,g51)
    c: Coincident(g80,g51)
    c: Coincident(g80,g75)
    c: Weight(g81) = 1
    c: Equal(g81,g82)
    c: Equal(g81,g83)
    c: InternalAlignment(g81,g84)
    c: InternalAlignment(g82,g84)
    c: InternalAlignment(g83,g84)
    c: InternalAlignment(g85,g84)
    c: InternalAlignment(g86,g84)
    c: Weight(g87) = 1
    c: Equal(g87,g88)
    c: Equal(g87,g89)
    c: InternalAlignment(g87,g90)
    c: InternalAlignment(g88,g90)
    c: InternalAlignment(g89,g90)
    c: InternalAlignment(g91,g90)
    c: InternalAlignment(g92,g90)
    c: Block(g84)
    c: Block(g90)
    c: Coincident(g93,g84)
    c: Coincident(g93,g90)
    c: Vertical(g93)
    c: Coincident(g94,g84)
    c: Coincident(g94,g45)
    c: Coincident(g95,g45)
    c: Coincident(g95,g90)
    c: Weight(g96) = 1
    c: Equal(g96,g97)
    c: Equal(g96,g98)
    c: InternalAlignment(g96,g99)
    c: InternalAlignment(g97,g99)
    c: InternalAlignment(g98,g99)
    c: InternalAlignment(g100,g99)
    c: InternalAlignment(g101,g99)
    c: Weight(g102) = 1
    c: Equal(g102,g103)
    c: Equal(g102,g104)
    c: InternalAlignment(g102,g105)
    c: InternalAlignment(g103,g105)
    c: InternalAlignment(g104,g105)
    c: InternalAlignment(g106,g105)
    c: InternalAlignment(g107,g105)
    c: Block(g99)
    c: Block(g105)
    c: Coincident(g108,g99)
    c: Coincident(g108,g105)
    c: Vertical(g108)
    c: Coincident(g109,g105)
    c: Coincident(g109,g63)
    c: Coincident(g110,g63)
    c: Coincident(g110,g99)
    c: Weight(g111) = 1
    c: Equal(g111,g112)
    c: Equal(g111,g113)
    c: InternalAlignment(g111,g114)
    c: InternalAlignment(g112,g114)
    c: InternalAlignment(g113,g114)
    c: InternalAlignment(g115,g114)
    c: InternalAlignment(g116,g114)
    c: Weight(g117) = 1
    c: Equal(g117,g118)
    c: Equal(g117,g119)
    c: InternalAlignment(g117,g120)
    c: InternalAlignment(g118,g120)
    c: InternalAlignment(g119,g120)
    c: InternalAlignment(g121,g120)
    c: InternalAlignment(g122,g120)
    c: Block(g114)
    c: Block(g120)
    c: Coincident(g123,g114)
    c: Coincident(g123,g120)
    c: Vertical(g123)
    c: Coincident(g124,g120)
    c: Coincident(g124,g57)
    c: Coincident(g125,g57)
    c: Coincident(g125,g114)
    c: Weight(g126) = 1
    c: Equal(g126,g127)
    c: Equal(g126,g128)
    c: InternalAlignment(g126,g129)
    c: InternalAlignment(g127,g129)
    c: InternalAlignment(g128,g129)
    c: InternalAlignment(g130,g129)
    c: InternalAlignment(g131,g129)
    c: Weight(g132) = 1
    c: Equal(g132,g133)
    c: Equal(g132,g134)
    c: InternalAlignment(g132,g135)
    c: InternalAlignment(g133,g135)
    c: InternalAlignment(g134,g135)
    c: InternalAlignment(g136,g135)
    c: InternalAlignment(g137,g135)
    c: Weight(g138) = 1
    c: Equal(g138,g139)
    c: Equal(g138,g140)
    c: InternalAlignment(g138,g141)
    c: InternalAlignment(g139,g141)
    c: InternalAlignment(g140,g141)
    c: InternalAlignment(g142,g141)
    c: InternalAlignment(g143,g141)
    c: Weight(g144) = 1
    c: Equal(g144,g145)
    c: Equal(g144,g146)
    c: InternalAlignment(g144,g147)
    c: InternalAlignment(g145,g147)
    c: InternalAlignment(g146,g147)
    c: InternalAlignment(g148,g147)
    c: InternalAlignment(g149,g147)
    c: Block(g147)
    c: Block(g141)
    c: Block(g135)
    c: Block(g129)
    c: Coincident(g150,g25)
    c: Coincident(g150,g147)
    c: Coincident(g151,g147)
    c: Coincident(g151,g141)
    c: Horizontal(g151)
    c: Coincident(g152,g141)
    c: Coincident(g152,g25)
    c: Vertical(g152)
    c: Coincident(g153,g19)
    c: Coincident(g153,g135)
    c: Vertical(g153)
    c: Coincident(g154,g135)
    c: Coincident(g154,g129)
    c: Horizontal(g154)
    c: Coincident(g155,g129)
    c: Coincident(g155,g19)
    c: Weight(g156) = 1
    c: Equal(g156,g157)
    c: Equal(g156,g158)
    c: InternalAlignment(g156,g159)
    c: InternalAlignment(g157,g159)
    c: InternalAlignment(g158,g159)
    c: InternalAlignment(g160,g159)
    c: InternalAlignment(g161,g159)
    c: Weight(g162) = 1
    c: Equal(g162,g163)
    c: Equal(g162,g164)
    c: InternalAlignment(g162,g165)
    c: InternalAlignment(g163,g165)
    c: InternalAlignment(g164,g165)
    c: InternalAlignment(g166,g165)
    c: InternalAlignment(g167,g165)
    c: Weight(g168) = 1
    c: Equal(g168,g169)
    c: Equal(g168,g170)
    c: InternalAlignment(g168,g171)
    c: InternalAlignment(g169,g171)
    c: InternalAlignment(g170,g171)
    c: InternalAlignment(g172,g171)
    c: InternalAlignment(g173,g171)
    c: Weight(g174) = 1
    c: Equal(g174,g175)
    c: Equal(g174,g176)
    c: InternalAlignment(g174,g177)
    c: InternalAlignment(g175,g177)
    c: InternalAlignment(g176,g177)
    c: InternalAlignment(g178,g177)
    c: InternalAlignment(g179,g177)
    c: Block(g177)
    c: Block(g171)
    c: Block(g165)
    c: Block(g159)
    c: Coincident(g180,g177)
    c: Coincident(g180,g171)
    c: Horizontal(g180)
    c: Coincident(g181,g171)
    c: Coincident(g181,g7)
    c: Vertical(g181)
    c: Coincident(g182,g13)
    c: Coincident(g182,g165)
    c: Vertical(g182)
    c: Coincident(g183,g165)
    c: Coincident(g183,g159)
    c: Horizontal(g183)
    c: Coincident(g184,g159)
    c: Coincident(g184,g13)
    c: Coincident(g185,g7)
    c: Weight(g186) = 1
    c: Equal(g186,g187)
    c: Equal(g186,g188)
    c: InternalAlignment(g186,g189)
    c: InternalAlignment(g187,g189)
    c: InternalAlignment(g188,g189)
    c: InternalAlignment(g190,g189)
    c: InternalAlignment(g191,g189)
    c: Weight(g192) = 1
    c: Equal(g192,g193)
    c: Equal(g192,g194)
    c: InternalAlignment(g192,g195)
    c: InternalAlignment(g193,g195)
    c: InternalAlignment(g194,g195)
    c: InternalAlignment(g196,g195)
    c: InternalAlignment(g197,g195)
    c: Block(g195)
    c: Block(g189)
    c: Coincident(g198,g195)
    c: Coincident(g198,g31)
    c: Coincident(g199,g31)
    c: Coincident(g199,g189)
    c: Coincident(g200,g189)
    c: Coincident(g200,g195)
    c: Vertical(g200)
    c: Weight(g201) = 1
    c: Equal(g201,g202)
    c: Equal(g201,g203)
    c: InternalAlignment(g201,g204)
    c: InternalAlignment(g202,g204)
    c: InternalAlignment(g203,g204)
    c: InternalAlignment(g205,g204)
    c: InternalAlignment(g206,g204)
    c: Weight(g207) = 1
    c: Equal(g207,g208)
    c: Equal(g207,g209)
    c: InternalAlignment(g207,g210)
    c: InternalAlignment(g208,g210)
    c: InternalAlignment(g209,g210)
    c: InternalAlignment(g211,g210)
    c: InternalAlignment(g212,g210)
    c: Block(g210)
    c: Block(g204)
    c: Coincident(g213,g204)
    c: Coincident(g213,g37)
    c: Coincident(g214,g37)
    c: Coincident(g214,g210)
    c: Coincident(g215,g210)
    c: Coincident(g215,g204)
    c: Vertical(g215)
    c: Horizontal(g216)
    c: Block(g216)
    c: Vertical(g217)
    c: Block(g217)
    c: Block(g218)
    c: Weight(g219) = 1
    c: Equal(g219,g220)
    c: Equal(g219,g221)
    c: InternalAlignment(g219,g222)
    c: InternalAlignment(g220,g222)
    c: InternalAlignment(g221,g222)
    c: InternalAlignment(g223,g222)
    c: InternalAlignment(g224,g222)
    c: Weight(g225) = 1
    c: Equal(g225,g226)
    c: Equal(g225,g227)
    c: InternalAlignment(g225,g228)
    c: InternalAlignment(g226,g228)
    c: InternalAlignment(g227,g228)
    c: InternalAlignment(g229,g228)
    c: InternalAlignment(g230,g228)
    c: Weight(g231) = 1
    c: Equal(g231,g232)
    c: Equal(g231,g233)
    c: InternalAlignment(g231,g234)
    c: InternalAlignment(g232,g234)
    c: InternalAlignment(g233,g234)
    c: InternalAlignment(g235,g234)
    c: InternalAlignment(g236,g234)
    c: Weight(g237) = 1
    c: Equal(g237,g238)
    c: Equal(g237,g239)
    c: InternalAlignment(g237,g240)
    c: InternalAlignment(g238,g240)
    c: InternalAlignment(g239,g240)
    c: InternalAlignment(g241,g240)
    c: InternalAlignment(g242,g240)
    c: Block(g222)
    c: Block(g228)
    c: Block(g234)
    c: Block(g240)
    c: Coincident(g243,g228)
    c: Coincident(g243,g222)
    c: Horizontal(g243)
    c: Block(g185)
    c: Weight(g244) = 1
    c: Equal(g244,g245)
    c: Equal(g244,g246)
    c: InternalAlignment(g244,g247)
    c: InternalAlignment(g245,g247)
    c: InternalAlignment(g246,g247)
    c: InternalAlignment(g248,g247)
    c: InternalAlignment(g249,g247)
    c: Weight(g250) = 1
    c: Equal(g250,g251)
    c: Equal(g250,g252)
    c: InternalAlignment(g250,g253)
    c: InternalAlignment(g251,g253)
    c: InternalAlignment(g252,g253)
    c: InternalAlignment(g254,g253)
    c: InternalAlignment(g255,g253)
    c: Block(g247)
    c: Block(g253)
    c: Coincident(g256,g247)
    c: Coincident(g256,g253)
    c: Weight(g257) = 1
    c: Equal(g257,g258)
    c: Equal(g257,g259)
    c: InternalAlignment(g257,g260)
    c: InternalAlignment(g258,g260)
    c: InternalAlignment(g259,g260)
    c: InternalAlignment(g261,g260)
    c: InternalAlignment(g262,g260)
    c: Weight(g263) = 1
    c: Equal(g263,g264)
    c: Equal(g263,g265)
    c: InternalAlignment(g263,g266)
    c: InternalAlignment(g264,g266)
    c: InternalAlignment(g265,g266)
    c: InternalAlignment(g267,g266)
    c: InternalAlignment(g268,g266)
    c: Weight(g269) = 1
    c: Equal(g269,g270)
    c: Equal(g269,g271)
    c: InternalAlignment(g269,g272)
    c: InternalAlignment(g270,g272)
    c: InternalAlignment(g271,g272)
    c: InternalAlignment(g273,g272)
    c: InternalAlignment(g274,g272)
    c: Block(g272)
    c: Block(g266)
    c: Block(g260)
    c: Coincident(g275,g266)
    c: Coincident(g275,g260)
    c: Coincident(g276,g260)
    c: Coincident(g276,g272)
    c: Vertical(g276)
    c: Coincident(g277,g272)
    c: Coincident(g277,g266)
    c: Horizontal(g277)
    c: Weight(g278) = 1
    c: Equal(g278,g279)
    c: InternalAlignment(g278,g280)
    c: InternalAlignment(g279,g280)
    c: InternalAlignment(g281,g280)
    c: InternalAlignment(g282,g280)
    c: Weight(g283) = 1
    c: InternalAlignment(g284,g286)
    c: InternalAlignment(g285,g286)
    c: InternalAlignment(g287,g286)
    c: InternalAlignment(g288,g286)
    c: Weight(g289) = 1
    c: Equal(g289,g290)
    c: Equal(g289,g291)
    c: InternalAlignment(g289,g292)
    c: InternalAlignment(g290,g292)
    c: InternalAlignment(g291,g292)
    c: InternalAlignment(g293,g292)
    c: InternalAlignment(g294,g292)
    c: Equal(g295,g296)
    c: Equal(g295,g297)
    c: InternalAlignment(g295,g298)
    c: InternalAlignment(g296,g298)
    c: InternalAlignment(g297,g298)
    c: InternalAlignment(g299,g298)
    c: InternalAlignment(g300,g298)
    c: Block(g286)
    c: Block(g292)
    c: Block(g298)
    c: Block(g280)
    c: Coincident(g301,g280)
    c: Coincident(g301,g286)
    c: Horizontal(g301)
    c: Coincident(g302,g286)
    c: Coincident(g302,g292)
    c: Vertical(g302)
    c: Coincident(g303,g292)
    c: Coincident(g303,g298)
    c: Horizontal(g303)
    c: Coincident(g304,g298)
    c: Coincident(g304,g280)
    c: Weight(g305) = 1
    c: Equal(g305,g306)
    c: Equal(g305,g307)
    c: InternalAlignment(g305,g308)
    c: InternalAlignment(g306,g308)
    c: InternalAlignment(g307,g308)
    c: InternalAlignment(g309,g308)
    c: InternalAlignment(g310,g308)
    c: Weight(g311) = 1
    c: Equal(g311,g312)
    c: Equal(g311,g313)
    c: InternalAlignment(g311,g314)
    c: InternalAlignment(g312,g314)
    c: InternalAlignment(g313,g314)
    c: InternalAlignment(g315,g314)
    c: InternalAlignment(g316,g314)
    c: Weight(g317) = 1
    c: Equal(g317,g318)
    c: Equal(g317,g319)
    c: InternalAlignment(g317,g320)
    c: InternalAlignment(g318,g320)
    c: InternalAlignment(g319,g320)
    c: InternalAlignment(g321,g320)
    c: InternalAlignment(g322,g320)
    c: Block(g320)
    c: Block(g314)
    c: Block(g308)
    c: Coincident(g323,g320)
    c: Coincident(g323,g314)
    c: Horizontal(g323)
    c: Coincident(g324,g314)
    c: Coincident(g324,g308)
    c: Vertical(g324)
    c: Coincident(g325,g308)
    c: Coincident(g325,g320)
    c: InternalAlignment(g326,g327)
    c: InternalAlignment(g328,g327)
    c: InternalAlignment(g329,g327)
    c: Block(g327)
    c: Equal(g330,g331)
    c: Equal(g330,g332)
    c: InternalAlignment(g330,g333)
    c: InternalAlignment(g331,g333)
    c: InternalAlignment(g332,g333)
    c: InternalAlignment(g334,g333)
    c: InternalAlignment(g335,g333)
    c: Block(g333)
    c: Coincident(g336,g327)
    c: Horizontal(g336)
    c: Block(g336)
    c: Coincident(g337,g327)
    c: Coincident(g337,g253)
    c: Vertical(g337)
    c: Coincident(g338,g333)
    c: Coincident(g338,g247)
    c: Vertical(g338)
    c: Block(g339)
    c: Block(g2)
    c: Distance(g337) = 119.89
    c: Coincident(g340,g339)
    c: Coincident(g340,g2)
    c: Coincident(g341,g2)
    c: Coincident(g341,g339)
    c: Block(g3)
    c: Block(g342)
    c: Coincident(g343,g342)
    c: Coincident(g343,g3)
    c: Coincident(g344,g342)
    c: Coincident(g344,g3)
    c: Block(g344)
    c: Block(g343)
    c: Weight(g345) = 1
    c: Equal(g345,g346)
    c: Equal(g345,g347)
    c: InternalAlignment(g345,g348)
    c: InternalAlignment(g346,g348)
    c: InternalAlignment(g347,g348)
    c: InternalAlignment(g349,g348)
    c: InternalAlignment(g350,g348)
    c: Weight(g351) = 1
    c: Equal(g351,g352)
    c: Equal(g351,g353)
    c: InternalAlignment(g351,g354)
    c: InternalAlignment(g352,g354)
    c: InternalAlignment(g353,g354)
    c: InternalAlignment(g355,g354)
    c: InternalAlignment(g356,g354)
    c: Weight(g357) = 1
    c: Equal(g357,g358)
    c: Equal(g357,g359)
    c: InternalAlignment(g357,g360)
    c: InternalAlignment(g358,g360)
    c: InternalAlignment(g359,g360)
    c: InternalAlignment(g361,g360)
    c: InternalAlignment(g362,g360)
    c: Weight(g363) = 1
    c: Equal(g363,g364)
    c: Equal(g363,g365)
    c: InternalAlignment(g363,g366)
    c: InternalAlignment(g364,g366)
    c: InternalAlignment(g365,g366)
    c: InternalAlignment(g367,g366)
    c: InternalAlignment(g368,g366)
    c: Block(g366)
    c: Block(g360)
    c: Block(g354)
    c: Block(g348)
    c: Coincident(g369,g366)
    c: Coincident(g369,g348)
    c: Vertical(g369)
    c: Coincident(g370,g348)
    c: Coincident(g370,g354)
    c: Coincident(g371,g354)
    c: Coincident(g371,g360)
    c: Vertical(g371)
    c: Coincident(g372,g360)
    c: Coincident(g372,g366)
    c: Horizontal(g372)
    c: Vertical(g373)
    c: PointOnObject(g373,g41)
    c: Horizontal(g374)
    c: Distance(g374) = 50
    c: Horizontal(g375)
    c: Equal(g374,g375) = 50
FEATURE [Part::Extrusion] Extrude005
  Base = -> Sketch003
  Dir = (0,0,1)
  DirMode = 2
  FaceMakerClass = Part::FaceMakerBullseye
  LengthFwd = 24
  LengthRev = 0
  Solid = true
  Symmetric = false
